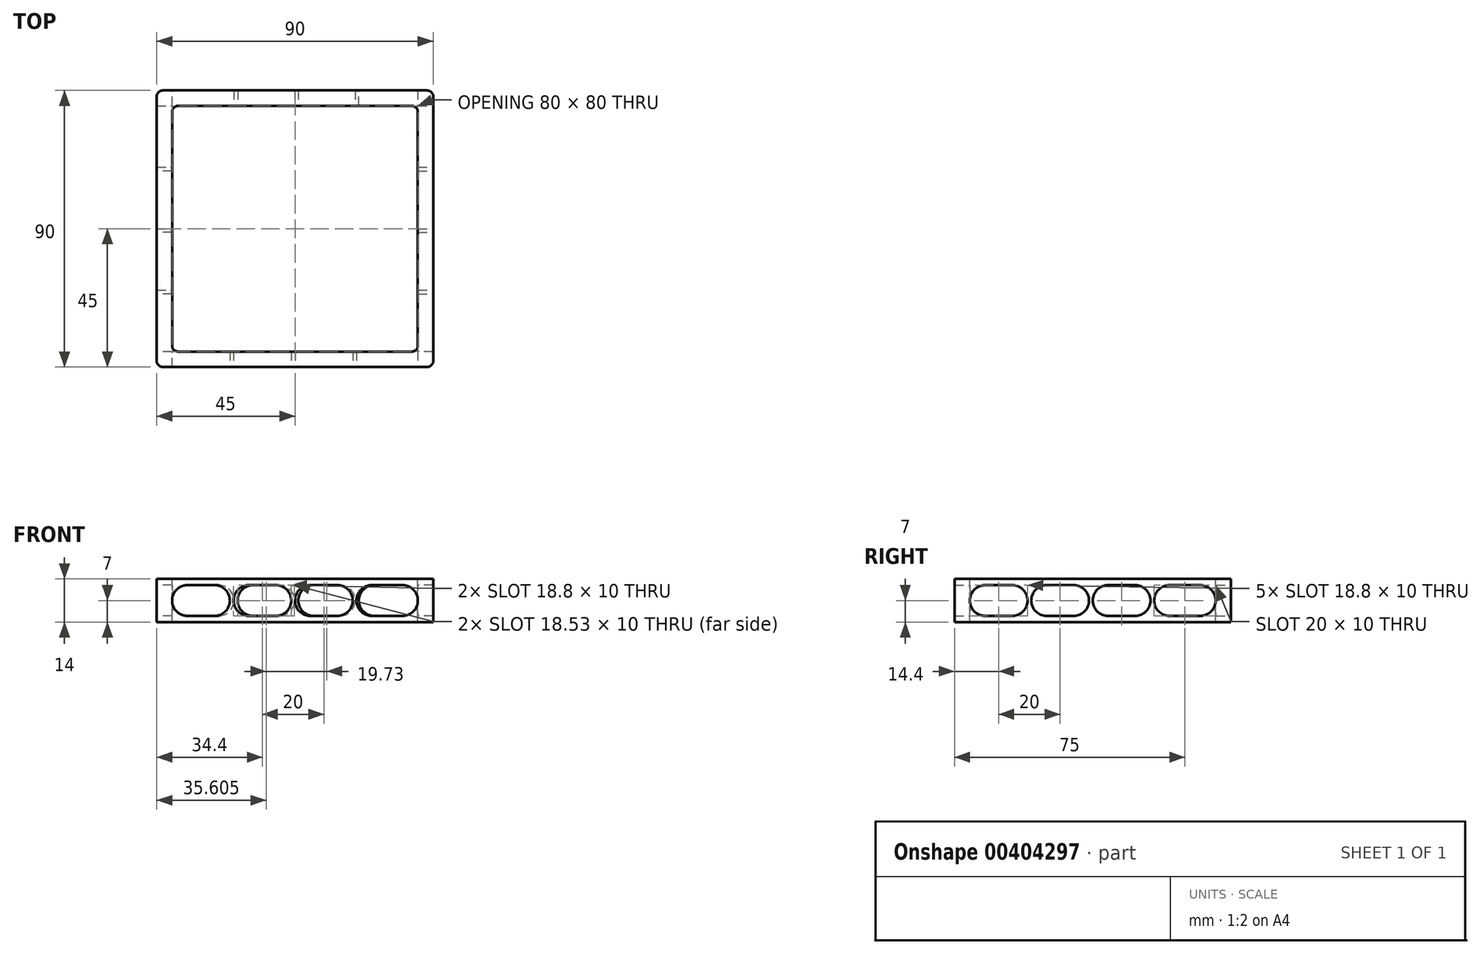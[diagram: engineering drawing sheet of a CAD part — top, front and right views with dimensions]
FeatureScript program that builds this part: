
annotation { "Feature Type Name" : "Feature", "Feature Type Description" : "" }
export const myFeature = defineFeature(function(context is Context, id is Id, definition is map)
    precondition{}
    {
        {
            var Q0;
            Q0=qCreatedBy(makeId("Front.planeOp"),FACE);
            var sketch = newSketch(context, id + "F0", { "sketchPlane" : qUnion([Q0])});
            skLineSegment(sketch, "E0.bottom", {"start": v(-45, 7) * mm, "end": v(45, 7) * mm});
            skLineSegment(sketch, "E0.top", {"start": v(-45, -7) * mm, "end": v(45, -7) * mm});
            skLineSegment(sketch, "E0.left", {"start": v(-45, 7) * mm, "end": v(-45, -7) * mm});
            skLineSegment(sketch, "E0.right", {"start": v(45, 7) * mm, "end": v(45, -7) * mm});
            skPoint(sketch, "E0.middle", {"position": v(0, 0) * mm});
            skSolve(sketch);
        }
        {
            var Q0;
            Q0=qSketchRegion(id+"F0",true);
            extrude(context, id + "F1", {"entities" : qUnion([Q0]), "endBound" : BoundingType.SYMMETRIC, "depth" : 90 * mm});
        }
        {
            var Q0;
            Q0=makeQuery(id+"F1.opExtrude","CAP_FACE",FACE,{"disambiguationData":[OSD([sQuery(id+"F0.wireOp",EDGE,"E0.bottom"),sQuery(id+"F0.wireOp",EDGE,"E0.top"),sQuery(id+"F0.wireOp",EDGE,"E0.left"),sQuery(id+"F0.wireOp",EDGE,"E0.right")])],"isStart":false});
            var sketch = newSketch(context, id + "F2", { "sketchPlane" : qUnion([Q0])});
            skLineSegment(sketch, "E1.bottom", {"start": v(-40, 5) * mm, "end": v(40, 5) * mm});
            skLineSegment(sketch, "E1.top", {"start": v(-40, -5) * mm, "end": v(40, -5) * mm});
            skLineSegment(sketch, "E1.left", {"start": v(-40, 5) * mm, "end": v(-40, -5) * mm});
            skLineSegment(sketch, "E1.right", {"start": v(40, 5) * mm, "end": v(40, -5) * mm});
            skPoint(sketch, "E1.middle", {"position": v(0, 0) * mm});
            skSolve(sketch);
        }
        {
            var Q0;
            Q0=qSketchRegion(id+"F2",true);
            extrude(context, id + "F3", {"entities" : qUnion([Q0]), "operationType" : NewBodyOperationType.REMOVE, "oppositeDirection" : true, "depth" : 90 * mm});
        }
        {
            var Q0;
            Q0=makeQuery(id+"F1.opExtrude","SWEPT_FACE",FACE,{"disambiguationData":[OSD([sQuery(id+"F0.wireOp",EDGE,"E0.right")])]});
            var sketch = newSketch(context, id + "F4", { "sketchPlane" : qUnion([Q0])});
            skLineSegment(sketch, "E2.bottom", {"start": v(-40, 5) * mm, "end": v(40, 5) * mm});
            skLineSegment(sketch, "E2.top", {"start": v(-40, -5) * mm, "end": v(40, -5) * mm});
            skLineSegment(sketch, "E2.left", {"start": v(-40, 5) * mm, "end": v(-40, -5) * mm});
            skLineSegment(sketch, "E2.right", {"start": v(40, 5) * mm, "end": v(40, -5) * mm});
            skPoint(sketch, "E2.middle", {"position": v(0, 0) * mm});
            skSolve(sketch);
        }
        {
            var Q0;
            Q0=qSketchRegion(id+"F4",true);
            extrude(context, id + "F5", {"entities" : qUnion([Q0]), "operationType" : NewBodyOperationType.REMOVE, "oppositeDirection" : true, "depth" : 90 * mm});
        }
        {
            var Q0;
            Q0=makeQuery(id+"F1.opExtrude","SWEPT_FACE",FACE,{"disambiguationData":[OSD([sQuery(id+"F0.wireOp",EDGE,"E0.bottom")])]});
            var sketch = newSketch(context, id + "F6", { "sketchPlane" : qUnion([Q0])});
            skLineSegment(sketch, "E3.bottom", {"start": v(-40, 40) * mm, "end": v(40, 40) * mm});
            skLineSegment(sketch, "E3.top", {"start": v(-40, -40) * mm, "end": v(40, -40) * mm});
            skLineSegment(sketch, "E3.left", {"start": v(-40, 40) * mm, "end": v(-40, -40) * mm});
            skLineSegment(sketch, "E3.right", {"start": v(40, 40) * mm, "end": v(40, -40) * mm});
            skSolve(sketch);
        }
        {
            var Q0;
            Q0=qSketchRegion(id+"F6",true);
            extrude(context, id + "F7", {"entities" : qUnion([Q0]), "operationType" : NewBodyOperationType.REMOVE, "oppositeDirection" : true, "depth" : 14 * mm});
        }
        {
            var Q0;
            {var subQ3=sQuery(id+"F6.wireOp",EDGE,"E3.bottom");var subQ4=sQuery(id+"F6.wireOp",EDGE,"E3.left");Q0=makeQuery(id+"F7.boolean.opBoolean","COPY",EDGE,{"disambiguationData":[TD([makeQuery(id+"F1.opExtrude","SWEPT_FACE",FACE,{"disambiguationData":[OSD([sQuery(id+"F0.wireOp",EDGE,"E0.bottom")])]})])],"derivedFrom":makeQuery(id+"F7.opExtrude","SWEPT_EDGE",EDGE,{"disambiguationData":[OSD([subQ3,subQ4])]})});}
            var Q1;
            {var subQ3=sQuery(id+"F6.wireOp",EDGE,"E3.bottom");var subQ4=sQuery(id+"F6.wireOp",EDGE,"E3.left");Q1=makeQuery(id+"F7.boolean.opBoolean","COPY",EDGE,{"disambiguationData":[TD([makeQuery(id+"F1.opExtrude","SWEPT_FACE",FACE,{"disambiguationData":[OSD([sQuery(id+"F0.wireOp",EDGE,"E0.top")])]})])],"derivedFrom":makeQuery(id+"F7.opExtrude","SWEPT_EDGE",EDGE,{"disambiguationData":[OSD([subQ3,subQ4])]})});}
            var Q2;
            {var subQ3=sQuery(id+"F6.wireOp",EDGE,"E3.top");var subQ4=sQuery(id+"F6.wireOp",EDGE,"E3.left");Q2=makeQuery(id+"F7.boolean.opBoolean","COPY",EDGE,{"disambiguationData":[TD([makeQuery(id+"F1.opExtrude","SWEPT_FACE",FACE,{"disambiguationData":[OSD([sQuery(id+"F0.wireOp",EDGE,"E0.top")])]})])],"derivedFrom":makeQuery(id+"F7.opExtrude","SWEPT_EDGE",EDGE,{"disambiguationData":[OSD([subQ3,subQ4])]})});}
            var Q3;
            {var subQ3=sQuery(id+"F6.wireOp",EDGE,"E3.top");var subQ4=sQuery(id+"F6.wireOp",EDGE,"E3.left");Q3=makeQuery(id+"F7.boolean.opBoolean","COPY",EDGE,{"disambiguationData":[TD([makeQuery(id+"F1.opExtrude","SWEPT_FACE",FACE,{"disambiguationData":[OSD([sQuery(id+"F0.wireOp",EDGE,"E0.bottom")])]})])],"derivedFrom":makeQuery(id+"F7.opExtrude","SWEPT_EDGE",EDGE,{"disambiguationData":[OSD([subQ3,subQ4])]})});}
            var Q4;
            {var subQ3=sQuery(id+"F6.wireOp",EDGE,"E3.right");var subQ4=sQuery(id+"F6.wireOp",EDGE,"E3.top");Q4=makeQuery(id+"F7.boolean.opBoolean","COPY",EDGE,{"disambiguationData":[TD([makeQuery(id+"F1.opExtrude","SWEPT_FACE",FACE,{"disambiguationData":[OSD([sQuery(id+"F0.wireOp",EDGE,"E0.bottom")])]})])],"derivedFrom":makeQuery(id+"F7.opExtrude","SWEPT_EDGE",EDGE,{"disambiguationData":[OSD([subQ4,subQ3])]})});}
            var Q5;
            {var subQ3=sQuery(id+"F6.wireOp",EDGE,"E3.top");var subQ4=sQuery(id+"F6.wireOp",EDGE,"E3.right");Q5=makeQuery(id+"F7.boolean.opBoolean","COPY",EDGE,{"disambiguationData":[TD([makeQuery(id+"F1.opExtrude","SWEPT_FACE",FACE,{"disambiguationData":[OSD([sQuery(id+"F0.wireOp",EDGE,"E0.top")])]})])],"derivedFrom":makeQuery(id+"F7.opExtrude","SWEPT_EDGE",EDGE,{"disambiguationData":[OSD([subQ3,subQ4])]})});}
            var Q6;
            {var subQ3=sQuery(id+"F6.wireOp",EDGE,"E3.right");var subQ4=sQuery(id+"F6.wireOp",EDGE,"E3.bottom");Q6=makeQuery(id+"F7.boolean.opBoolean","COPY",EDGE,{"disambiguationData":[TD([makeQuery(id+"F1.opExtrude","SWEPT_FACE",FACE,{"disambiguationData":[OSD([sQuery(id+"F0.wireOp",EDGE,"E0.bottom")])]})])],"derivedFrom":makeQuery(id+"F7.opExtrude","SWEPT_EDGE",EDGE,{"disambiguationData":[OSD([subQ4,subQ3])]})});}
            var Q7;
            {var subQ3=sQuery(id+"F6.wireOp",EDGE,"E3.bottom");var subQ4=sQuery(id+"F6.wireOp",EDGE,"E3.right");Q7=makeQuery(id+"F7.boolean.opBoolean","COPY",EDGE,{"disambiguationData":[TD([makeQuery(id+"F1.opExtrude","SWEPT_FACE",FACE,{"disambiguationData":[OSD([sQuery(id+"F0.wireOp",EDGE,"E0.top")])]})])],"derivedFrom":makeQuery(id+"F7.opExtrude","SWEPT_EDGE",EDGE,{"disambiguationData":[OSD([subQ3,subQ4])]})});}
            var Q8;
            Q8=makeQuery(id+"F1.opExtrude","CAP_EDGE",EDGE,{"disambiguationData":[OSD([sQuery(id+"F0.wireOp",EDGE,"E0.left")])],"isStart":false});
            var Q9;
            Q9=makeQuery(id+"F1.opExtrude","CAP_EDGE",EDGE,{"disambiguationData":[OSD([sQuery(id+"F0.wireOp",EDGE,"E0.right")])],"isStart":false});
            var Q10;
            Q10=makeQuery(id+"F1.opExtrude","CAP_EDGE",EDGE,{"disambiguationData":[OSD([sQuery(id+"F0.wireOp",EDGE,"E0.right")])],"isStart":true});
            var Q11;
            Q11=makeQuery(id+"F1.opExtrude","CAP_EDGE",EDGE,{"disambiguationData":[OSD([sQuery(id+"F0.wireOp",EDGE,"E0.left")])],"isStart":true});
            fillet(context, id + "F8", {"entities" : qUnion([Q0, Q1, Q2, Q3, Q4, Q5, Q6, Q7, Q8, Q9, Q10, Q11]), "radius" : 2 * mm, "allowEdgeOverflow" : false});
        }
        {
            var Q0;
            {var subQ0=sQuery(id+"F2.wireOp",EDGE,"E1.top");var subQ1=sQuery(id+"F2.wireOp",EDGE,"E1.right");Q0=makeQuery(id+"F5.boolean.opBoolean","SPLIT",EDGE,{"disambiguationData":[TD([makeQuery(id+"F5.opExtrude","SWEPT_FACE",FACE,{"disambiguationData":[OSD([sQuery(id+"F4.wireOp",EDGE,"E2.left")])]})])],"derivedFrom":makeQuery(id+"F3.boolean.opBoolean","COPY",EDGE,{"derivedFrom":makeQuery(id+"F3.opExtrude","SWEPT_EDGE",EDGE,{"disambiguationData":[OSD([subQ0,subQ1])]})})});}
            var Q1;
            {var subQ0=sQuery(id+"F2.wireOp",EDGE,"E1.bottom");var subQ1=sQuery(id+"F2.wireOp",EDGE,"E1.right");Q1=makeQuery(id+"F5.boolean.opBoolean","SPLIT",EDGE,{"disambiguationData":[TD([makeQuery(id+"F5.opExtrude","SWEPT_FACE",FACE,{"disambiguationData":[OSD([sQuery(id+"F4.wireOp",EDGE,"E2.left")])]})])],"derivedFrom":makeQuery(id+"F3.boolean.opBoolean","COPY",EDGE,{"derivedFrom":makeQuery(id+"F3.opExtrude","SWEPT_EDGE",EDGE,{"disambiguationData":[OSD([subQ0,subQ1])]})})});}
            var Q2;
            {var subQ0=sQuery(id+"F2.wireOp",EDGE,"E1.left");var subQ1=sQuery(id+"F2.wireOp",EDGE,"E1.top");Q2=makeQuery(id+"F5.boolean.opBoolean","SPLIT",EDGE,{"disambiguationData":[TD([makeQuery(id+"F5.opExtrude","SWEPT_FACE",FACE,{"disambiguationData":[OSD([sQuery(id+"F4.wireOp",EDGE,"E2.left")])]})])],"derivedFrom":makeQuery(id+"F3.boolean.opBoolean","COPY",EDGE,{"derivedFrom":makeQuery(id+"F3.opExtrude","SWEPT_EDGE",EDGE,{"disambiguationData":[OSD([subQ1,subQ0])]})})});}
            var Q3;
            {var subQ0=sQuery(id+"F2.wireOp",EDGE,"E1.left");var subQ1=sQuery(id+"F2.wireOp",EDGE,"E1.bottom");Q3=makeQuery(id+"F5.boolean.opBoolean","SPLIT",EDGE,{"disambiguationData":[TD([makeQuery(id+"F5.opExtrude","SWEPT_FACE",FACE,{"disambiguationData":[OSD([sQuery(id+"F4.wireOp",EDGE,"E2.left")])]})])],"derivedFrom":makeQuery(id+"F3.boolean.opBoolean","COPY",EDGE,{"derivedFrom":makeQuery(id+"F3.opExtrude","SWEPT_EDGE",EDGE,{"disambiguationData":[OSD([subQ1,subQ0])]})})});}
            var Q4;
            {var subQ0=sQuery(id+"F4.wireOp",EDGE,"E2.top");var subQ1=sQuery(id+"F4.wireOp",EDGE,"E2.left");Q4=makeQuery(id+"F5.boolean.opBoolean","COPY",EDGE,{"disambiguationData":[TD([makeQuery(id+"F1.opExtrude","SWEPT_FACE",FACE,{"disambiguationData":[OSD([sQuery(id+"F0.wireOp",EDGE,"E0.right")])]})])],"derivedFrom":makeQuery(id+"F5.opExtrude","SWEPT_EDGE",EDGE,{"disambiguationData":[OSD([subQ0,subQ1])]})});}
            var Q5;
            {var subQ0=sQuery(id+"F4.wireOp",EDGE,"E2.bottom");var subQ1=sQuery(id+"F4.wireOp",EDGE,"E2.left");Q5=makeQuery(id+"F5.boolean.opBoolean","COPY",EDGE,{"disambiguationData":[TD([makeQuery(id+"F1.opExtrude","SWEPT_FACE",FACE,{"disambiguationData":[OSD([sQuery(id+"F0.wireOp",EDGE,"E0.right")])]})])],"derivedFrom":makeQuery(id+"F5.opExtrude","SWEPT_EDGE",EDGE,{"disambiguationData":[OSD([subQ0,subQ1])]})});}
            var Q6;
            {var subQ0=sQuery(id+"F4.wireOp",EDGE,"E2.top");var subQ1=sQuery(id+"F4.wireOp",EDGE,"E2.right");Q6=makeQuery(id+"F5.boolean.opBoolean","COPY",EDGE,{"disambiguationData":[TD([makeQuery(id+"F1.opExtrude","SWEPT_FACE",FACE,{"disambiguationData":[OSD([sQuery(id+"F0.wireOp",EDGE,"E0.right")])]})])],"derivedFrom":makeQuery(id+"F5.opExtrude","SWEPT_EDGE",EDGE,{"disambiguationData":[OSD([subQ0,subQ1])]})});}
            var Q7;
            {var subQ0=sQuery(id+"F4.wireOp",EDGE,"E2.bottom");var subQ1=sQuery(id+"F4.wireOp",EDGE,"E2.right");Q7=makeQuery(id+"F5.boolean.opBoolean","COPY",EDGE,{"disambiguationData":[TD([makeQuery(id+"F1.opExtrude","SWEPT_FACE",FACE,{"disambiguationData":[OSD([sQuery(id+"F0.wireOp",EDGE,"E0.right")])]})])],"derivedFrom":makeQuery(id+"F5.opExtrude","SWEPT_EDGE",EDGE,{"disambiguationData":[OSD([subQ0,subQ1])]})});}
            var Q8;
            {var subQ0=sQuery(id+"F2.wireOp",EDGE,"E1.right");var subQ1=sQuery(id+"F2.wireOp",EDGE,"E1.top");Q8=makeQuery(id+"F5.boolean.opBoolean","SPLIT",EDGE,{"disambiguationData":[TD([makeQuery(id+"F5.opExtrude","SWEPT_FACE",FACE,{"disambiguationData":[OSD([sQuery(id+"F4.wireOp",EDGE,"E2.right")])]})])],"derivedFrom":makeQuery(id+"F3.boolean.opBoolean","COPY",EDGE,{"derivedFrom":makeQuery(id+"F3.opExtrude","SWEPT_EDGE",EDGE,{"disambiguationData":[OSD([subQ1,subQ0])]})})});}
            var Q9;
            {var subQ0=sQuery(id+"F2.wireOp",EDGE,"E1.right");var subQ1=sQuery(id+"F2.wireOp",EDGE,"E1.bottom");Q9=makeQuery(id+"F5.boolean.opBoolean","SPLIT",EDGE,{"disambiguationData":[TD([makeQuery(id+"F5.opExtrude","SWEPT_FACE",FACE,{"disambiguationData":[OSD([sQuery(id+"F4.wireOp",EDGE,"E2.right")])]})])],"derivedFrom":makeQuery(id+"F3.boolean.opBoolean","COPY",EDGE,{"derivedFrom":makeQuery(id+"F3.opExtrude","SWEPT_EDGE",EDGE,{"disambiguationData":[OSD([subQ1,subQ0])]})})});}
            var Q10;
            {var subQ0=sQuery(id+"F2.wireOp",EDGE,"E1.top");var subQ1=sQuery(id+"F2.wireOp",EDGE,"E1.left");Q10=makeQuery(id+"F5.boolean.opBoolean","SPLIT",EDGE,{"disambiguationData":[TD([makeQuery(id+"F5.opExtrude","SWEPT_FACE",FACE,{"disambiguationData":[OSD([sQuery(id+"F4.wireOp",EDGE,"E2.right")])]})])],"derivedFrom":makeQuery(id+"F3.boolean.opBoolean","COPY",EDGE,{"derivedFrom":makeQuery(id+"F3.opExtrude","SWEPT_EDGE",EDGE,{"disambiguationData":[OSD([subQ0,subQ1])]})})});}
            var Q11;
            {var subQ0=sQuery(id+"F4.wireOp",EDGE,"E2.top");var subQ1=sQuery(id+"F4.wireOp",EDGE,"E2.right");Q11=makeQuery(id+"F5.boolean.opBoolean","COPY",EDGE,{"disambiguationData":[TD([makeQuery(id+"F1.opExtrude","SWEPT_FACE",FACE,{"disambiguationData":[OSD([sQuery(id+"F0.wireOp",EDGE,"E0.left")])]})])],"derivedFrom":makeQuery(id+"F5.opExtrude","SWEPT_EDGE",EDGE,{"disambiguationData":[OSD([subQ0,subQ1])]})});}
            var Q12;
            {var subQ0=sQuery(id+"F4.wireOp",EDGE,"E2.top");var subQ1=sQuery(id+"F4.wireOp",EDGE,"E2.left");Q12=makeQuery(id+"F5.boolean.opBoolean","COPY",EDGE,{"disambiguationData":[TD([makeQuery(id+"F1.opExtrude","SWEPT_FACE",FACE,{"disambiguationData":[OSD([sQuery(id+"F0.wireOp",EDGE,"E0.left")])]})])],"derivedFrom":makeQuery(id+"F5.opExtrude","SWEPT_EDGE",EDGE,{"disambiguationData":[OSD([subQ0,subQ1])]})});}
            var Q13;
            {var subQ0=sQuery(id+"F4.wireOp",EDGE,"E2.bottom");var subQ1=sQuery(id+"F4.wireOp",EDGE,"E2.left");Q13=makeQuery(id+"F5.boolean.opBoolean","COPY",EDGE,{"disambiguationData":[TD([makeQuery(id+"F1.opExtrude","SWEPT_FACE",FACE,{"disambiguationData":[OSD([sQuery(id+"F0.wireOp",EDGE,"E0.left")])]})])],"derivedFrom":makeQuery(id+"F5.opExtrude","SWEPT_EDGE",EDGE,{"disambiguationData":[OSD([subQ0,subQ1])]})});}
            var Q14;
            {var subQ0=sQuery(id+"F2.wireOp",EDGE,"E1.bottom");var subQ1=sQuery(id+"F2.wireOp",EDGE,"E1.left");Q14=makeQuery(id+"F5.boolean.opBoolean","SPLIT",EDGE,{"disambiguationData":[TD([makeQuery(id+"F5.opExtrude","SWEPT_FACE",FACE,{"disambiguationData":[OSD([sQuery(id+"F4.wireOp",EDGE,"E2.right")])]})])],"derivedFrom":makeQuery(id+"F3.boolean.opBoolean","COPY",EDGE,{"derivedFrom":makeQuery(id+"F3.opExtrude","SWEPT_EDGE",EDGE,{"disambiguationData":[OSD([subQ0,subQ1])]})})});}
            var Q15;
            {var subQ0=sQuery(id+"F4.wireOp",EDGE,"E2.bottom");var subQ1=sQuery(id+"F4.wireOp",EDGE,"E2.right");Q15=makeQuery(id+"F5.boolean.opBoolean","COPY",EDGE,{"disambiguationData":[TD([makeQuery(id+"F1.opExtrude","SWEPT_FACE",FACE,{"disambiguationData":[OSD([sQuery(id+"F0.wireOp",EDGE,"E0.left")])]})])],"derivedFrom":makeQuery(id+"F5.opExtrude","SWEPT_EDGE",EDGE,{"disambiguationData":[OSD([subQ0,subQ1])]})});}
            fillet(context, id + "F9", {"entities" : qUnion([Q0, Q1, Q2, Q3, Q4, Q5, Q6, Q7, Q8, Q9, Q10, Q11, Q12, Q13, Q14, Q15]), "radius" : 5 * mm, "tangentPropagation" : true, "allowEdgeOverflow" : false});
        }
        {
            var Q0;
            Q0=makeQuery(id+"F1.opExtrude","SWEPT_FACE",FACE,{"disambiguationData":[OSD([sQuery(id+"F0.wireOp",EDGE,"E0.bottom")])]});
            var sketch = newSketch(context, id + "F10", { "sketchPlane" : qUnion([Q0])});
            skLineSegment(sketch, "E4.bottom", {"start": v(18.8, -40) * mm, "end": v(20, -40) * mm});
            skLineSegment(sketch, "E4.top", {"start": v(18.8, -45) * mm, "end": v(20, -45) * mm});
            skLineSegment(sketch, "E4.left", {"start": v(18.8, -40) * mm, "end": v(18.8, -45) * mm});
            skLineSegment(sketch, "E4.right", {"start": v(20, -40) * mm, "end": v(20, -45) * mm});
            skLineSegment(sketch, "E5.1.0.0", {"start": v(-1.2, -40) * mm, "end": v(-1.2, -45) * mm});
            skLineSegment(sketch, "E5.1.0.1", {"start": v(0, -40) * mm, "end": v(0, -45) * mm});
            skLineSegment(sketch, "E5.1.0.2", {"start": v(-1.2, -45) * mm, "end": v(0, -45) * mm});
            skLineSegment(sketch, "E5.1.0.3", {"start": v(-1.2, -40) * mm, "end": v(0, -40) * mm});
            skLineSegment(sketch, "E5.2.0.0", {"start": v(-21.2, -40) * mm, "end": v(-21.2, -45) * mm});
            skLineSegment(sketch, "E5.2.0.1", {"start": v(-20, -40) * mm, "end": v(-20, -45) * mm});
            skLineSegment(sketch, "E5.2.0.2", {"start": v(-21.2, -45) * mm, "end": v(-20, -45) * mm});
            skLineSegment(sketch, "E5.2.0.3", {"start": v(-21.2, -40) * mm, "end": v(-20, -40) * mm});
            skLineSegment(sketch, "E5.direction1", {"start": v(18.8, -45) * mm, "end": v(-1.2, -45) * mm, "construction": true});
            skLineSegment(sketch, "E6.0.1.0", {"start": v(19.6, 40) * mm, "end": v(-0.13, 40) * mm, "construction": true});
            skLineSegment(sketch, "E6.0.1.1", {"start": v(19.6, 40) * mm, "end": v(20.8, 40) * mm});
            skLineSegment(sketch, "E6.0.1.2", {"start": v(19.6, 45) * mm, "end": v(19.6, 40) * mm});
            skLineSegment(sketch, "E6.0.1.3", {"start": v(20.8, 45) * mm, "end": v(20.8, 40) * mm});
            skLineSegment(sketch, "E6.0.1.4", {"start": v(-29.6, 40) * mm, "end": v(-29.2, 40) * mm});
            skLineSegment(sketch, "E6.0.1.5", {"start": v(-29.6, 45) * mm, "end": v(-29.2, 45) * mm});
            skLineSegment(sketch, "E6.0.1.6", {"start": v(19.6, 45) * mm, "end": v(20.8, 45) * mm});
            skLineSegment(sketch, "E6.0.1.7", {"start": v(1.07, 45) * mm, "end": v(1.07, 40) * mm});
            skLineSegment(sketch, "E6.0.1.8", {"start": v(-0.13, 45) * mm, "end": v(1.07, 45) * mm});
            skLineSegment(sketch, "E6.0.1.9", {"start": v(-18.66, 45) * mm, "end": v(-18.66, 40) * mm});
            skLineSegment(sketch, "E6.0.1.10", {"start": v(-19.86, 40) * mm, "end": v(-18.66, 40) * mm});
            skLineSegment(sketch, "E6.0.1.11", {"start": v(-19.86, 45) * mm, "end": v(-18.66, 45) * mm});
            skLineSegment(sketch, "E6.0.1.14", {"start": v(-0.13, 45) * mm, "end": v(-0.13, 40) * mm});
            skLineSegment(sketch, "E6.0.1.15", {"start": v(-0.13, 40) * mm, "end": v(1.07, 40) * mm});
            skLineSegment(sketch, "E6.0.1.16", {"start": v(-19.86, 45) * mm, "end": v(-19.86, 40) * mm});
            skLineSegment(sketch, "E6.direction1", {"start": v(-29.6, -45) * mm, "end": v(-5, -45) * mm, "construction": true});
            skLineSegment(sketch, "E7.bottom", {"start": v(40, 18.8) * mm, "end": v(45, 18.8) * mm});
            skLineSegment(sketch, "E7.top", {"start": v(40, 20) * mm, "end": v(45, 20) * mm});
            skLineSegment(sketch, "E7.left", {"start": v(40, 18.8) * mm, "end": v(40, 20) * mm});
            skLineSegment(sketch, "E7.right", {"start": v(45, 18.8) * mm, "end": v(45, 20) * mm});
            skLineSegment(sketch, "E8.0.1.0", {"start": v(40, 0) * mm, "end": v(45, 0) * mm});
            skLineSegment(sketch, "E8.0.1.1", {"start": v(40, -1.2) * mm, "end": v(45, -1.2) * mm});
            skLineSegment(sketch, "E8.0.1.2", {"start": v(45, -1.2) * mm, "end": v(45, 0) * mm});
            skLineSegment(sketch, "E8.0.1.3", {"start": v(40, -1.2) * mm, "end": v(40, 0) * mm});
            skLineSegment(sketch, "E8.0.2.0", {"start": v(40, -20) * mm, "end": v(45, -20) * mm});
            skLineSegment(sketch, "E8.0.2.1", {"start": v(40, -21.2) * mm, "end": v(45, -21.2) * mm});
            skLineSegment(sketch, "E8.0.2.2", {"start": v(45, -21.2) * mm, "end": v(45, -20) * mm});
            skLineSegment(sketch, "E8.0.2.3", {"start": v(40, -21.2) * mm, "end": v(40, -20) * mm});
            skLineSegment(sketch, "E8.1.0.0", {"start": v(-45, 20) * mm, "end": v(-40, 20) * mm});
            skLineSegment(sketch, "E8.1.0.1", {"start": v(-45, 18.8) * mm, "end": v(-40, 18.8) * mm});
            skLineSegment(sketch, "E8.1.0.2", {"start": v(-40, 18.8) * mm, "end": v(-40, 20) * mm});
            skLineSegment(sketch, "E8.1.0.3", {"start": v(-45, 18.8) * mm, "end": v(-45, 20) * mm});
            skLineSegment(sketch, "E8.1.1.0", {"start": v(-45, 0) * mm, "end": v(-40, 0) * mm});
            skLineSegment(sketch, "E8.1.1.1", {"start": v(-45, -1.2) * mm, "end": v(-40, -1.2) * mm});
            skLineSegment(sketch, "E8.1.1.2", {"start": v(-40, -1.2) * mm, "end": v(-40, 0) * mm});
            skLineSegment(sketch, "E8.1.1.3", {"start": v(-45, -1.2) * mm, "end": v(-45, 0) * mm});
            skLineSegment(sketch, "E8.1.2.0", {"start": v(-45, -20) * mm, "end": v(-40, -20) * mm});
            skLineSegment(sketch, "E8.1.2.1", {"start": v(-45, -21.2) * mm, "end": v(-40, -21.2) * mm});
            skLineSegment(sketch, "E8.1.2.2", {"start": v(-40, -21.2) * mm, "end": v(-40, -20) * mm});
            skLineSegment(sketch, "E8.1.2.3", {"start": v(-45, -21.2) * mm, "end": v(-45, -20) * mm});
            skLineSegment(sketch, "E8.direction1", {"start": v(40, 18.8) * mm, "end": v(-45, 18.8) * mm, "construction": true});
            skLineSegment(sketch, "E8.direction2", {"start": v(40, 18.8) * mm, "end": v(40, -1.2) * mm, "construction": true});
            skSolve(sketch);
        }
        {
            var Q0;
            Q0=qSketchRegion(id+"F10",true);
            extrude(context, id + "F11", {"entities" : qUnion([Q0]), "operationType" : NewBodyOperationType.ADD, "oppositeDirection" : true, "depth" : 14 * mm});
        }
        {
            var Q0;
            {var subQ1=makeQuery(id+"F5.opExtrude","SWEPT_FACE",FACE,{"disambiguationData":[OSD([sQuery(id+"F4.wireOp",EDGE,"E2.top")])]});var subQ2=makeQuery(id+"F3.boolean.opBoolean","COPY",FACE,{"derivedFrom":makeQuery(id+"F3.opExtrude","SWEPT_FACE",FACE,{"disambiguationData":[OSD([sQuery(id+"F2.wireOp",EDGE,"E1.top")])]})});var subQ3=sQuery(id+"F0.wireOp",EDGE,"E0.left");var subQ4=makeQuery(id+"F1.opExtrude","SWEPT_FACE",FACE,{"disambiguationData":[OSD([subQ3])]});var subQ14=makeQuery(id+"F5.boolean.opBoolean","MERGE",FACE,{"derivedFrom":[subQ2,subQ1]});var subQ16=sQuery(id+"F0.wireOp",EDGE,"E0.right");var subQ17=makeQuery(id+"F1.opExtrude","SWEPT_FACE",FACE,{"disambiguationData":[OSD([subQ16])]});var subQ21=sQuery(id+"F0.wireOp",EDGE,"E0.top");var subQ22=sQuery(id+"F0.wireOp",EDGE,"E0.bottom");Q0=makeQuery(id+"F11.boolean.opBoolean","INTERSECT",EDGE,{"derivedFrom":[makeQuery(id+"F9.opFillet","SPLIT",FACE,{"disambiguationData":[OD(0.0)],"derivedFrom":makeQuery(id+"F8.opFillet","MERGE",FACE,{"derivedFrom":[makeQuery(id+"F7.boolean.opBoolean","SPLIT",FACE,{"disambiguationData":[TD([makeQuery(id+"F1.opExtrude","CAP_FACE",FACE,{"disambiguationData":[OSD([subQ22,subQ21,subQ3,subQ16])],"isStart":false})])],"derivedFrom":subQ14}),makeQuery(id+"F7.boolean.opBoolean","SPLIT",FACE,{"disambiguationData":[TD([makeQuery(id+"F1.opExtrude","CAP_FACE",FACE,{"disambiguationData":[OSD([subQ22,subQ21,subQ3,subQ16])],"isStart":true})])],"derivedFrom":subQ14}),makeQuery(id+"F7.boolean.opBoolean","SPLIT",FACE,{"disambiguationData":[TD([subQ17])],"derivedFrom":subQ14}),makeQuery(id+"F7.boolean.opBoolean","SPLIT",FACE,{"disambiguationData":[TD([subQ4])],"derivedFrom":subQ14})]})}),makeQuery(id+"F11.opExtrude","SWEPT_FACE",FACE,{"disambiguationData":[OSD([sQuery(id+"F10.wireOp",EDGE,"E4.right")])]})]});}
            var Q1;
            {var subQ1=makeQuery(id+"F5.opExtrude","SWEPT_FACE",FACE,{"disambiguationData":[OSD([sQuery(id+"F4.wireOp",EDGE,"E2.top")])]});var subQ2=makeQuery(id+"F3.boolean.opBoolean","COPY",FACE,{"derivedFrom":makeQuery(id+"F3.opExtrude","SWEPT_FACE",FACE,{"disambiguationData":[OSD([sQuery(id+"F2.wireOp",EDGE,"E1.top")])]})});var subQ3=sQuery(id+"F0.wireOp",EDGE,"E0.left");var subQ4=makeQuery(id+"F1.opExtrude","SWEPT_FACE",FACE,{"disambiguationData":[OSD([subQ3])]});var subQ14=makeQuery(id+"F5.boolean.opBoolean","MERGE",FACE,{"derivedFrom":[subQ2,subQ1]});var subQ16=sQuery(id+"F0.wireOp",EDGE,"E0.right");var subQ17=makeQuery(id+"F1.opExtrude","SWEPT_FACE",FACE,{"disambiguationData":[OSD([subQ16])]});var subQ21=sQuery(id+"F0.wireOp",EDGE,"E0.top");var subQ22=sQuery(id+"F0.wireOp",EDGE,"E0.bottom");Q1=makeQuery(id+"F11.boolean.opBoolean","INTERSECT",EDGE,{"derivedFrom":[makeQuery(id+"F9.opFillet","SPLIT",FACE,{"disambiguationData":[OD(0.0)],"derivedFrom":makeQuery(id+"F8.opFillet","MERGE",FACE,{"derivedFrom":[makeQuery(id+"F7.boolean.opBoolean","SPLIT",FACE,{"disambiguationData":[TD([makeQuery(id+"F1.opExtrude","CAP_FACE",FACE,{"disambiguationData":[OSD([subQ22,subQ21,subQ3,subQ16])],"isStart":false})])],"derivedFrom":subQ14}),makeQuery(id+"F7.boolean.opBoolean","SPLIT",FACE,{"disambiguationData":[TD([makeQuery(id+"F1.opExtrude","CAP_FACE",FACE,{"disambiguationData":[OSD([subQ22,subQ21,subQ3,subQ16])],"isStart":true})])],"derivedFrom":subQ14}),makeQuery(id+"F7.boolean.opBoolean","SPLIT",FACE,{"disambiguationData":[TD([subQ17])],"derivedFrom":subQ14}),makeQuery(id+"F7.boolean.opBoolean","SPLIT",FACE,{"disambiguationData":[TD([subQ4])],"derivedFrom":subQ14})]})}),makeQuery(id+"F11.opExtrude","SWEPT_FACE",FACE,{"disambiguationData":[OSD([sQuery(id+"F10.wireOp",EDGE,"E5.1.0.1")])]})]});}
            var Q2;
            {var subQ1=makeQuery(id+"F5.opExtrude","SWEPT_FACE",FACE,{"disambiguationData":[OSD([sQuery(id+"F4.wireOp",EDGE,"E2.top")])]});var subQ2=makeQuery(id+"F3.boolean.opBoolean","COPY",FACE,{"derivedFrom":makeQuery(id+"F3.opExtrude","SWEPT_FACE",FACE,{"disambiguationData":[OSD([sQuery(id+"F2.wireOp",EDGE,"E1.top")])]})});var subQ3=sQuery(id+"F0.wireOp",EDGE,"E0.left");var subQ4=makeQuery(id+"F1.opExtrude","SWEPT_FACE",FACE,{"disambiguationData":[OSD([subQ3])]});var subQ14=makeQuery(id+"F5.boolean.opBoolean","MERGE",FACE,{"derivedFrom":[subQ2,subQ1]});var subQ16=sQuery(id+"F0.wireOp",EDGE,"E0.right");var subQ17=makeQuery(id+"F1.opExtrude","SWEPT_FACE",FACE,{"disambiguationData":[OSD([subQ16])]});var subQ21=sQuery(id+"F0.wireOp",EDGE,"E0.top");var subQ22=sQuery(id+"F0.wireOp",EDGE,"E0.bottom");Q2=makeQuery(id+"F11.boolean.opBoolean","INTERSECT",EDGE,{"derivedFrom":[makeQuery(id+"F9.opFillet","SPLIT",FACE,{"disambiguationData":[OD(0.0)],"derivedFrom":makeQuery(id+"F8.opFillet","MERGE",FACE,{"derivedFrom":[makeQuery(id+"F7.boolean.opBoolean","SPLIT",FACE,{"disambiguationData":[TD([makeQuery(id+"F1.opExtrude","CAP_FACE",FACE,{"disambiguationData":[OSD([subQ22,subQ21,subQ3,subQ16])],"isStart":false})])],"derivedFrom":subQ14}),makeQuery(id+"F7.boolean.opBoolean","SPLIT",FACE,{"disambiguationData":[TD([makeQuery(id+"F1.opExtrude","CAP_FACE",FACE,{"disambiguationData":[OSD([subQ22,subQ21,subQ3,subQ16])],"isStart":true})])],"derivedFrom":subQ14}),makeQuery(id+"F7.boolean.opBoolean","SPLIT",FACE,{"disambiguationData":[TD([subQ17])],"derivedFrom":subQ14}),makeQuery(id+"F7.boolean.opBoolean","SPLIT",FACE,{"disambiguationData":[TD([subQ4])],"derivedFrom":subQ14})]})}),makeQuery(id+"F11.opExtrude","SWEPT_FACE",FACE,{"disambiguationData":[OSD([sQuery(id+"F10.wireOp",EDGE,"E5.2.0.1")])]})]});}
            var Q3;
            {var subQ1=makeQuery(id+"F5.opExtrude","SWEPT_FACE",FACE,{"disambiguationData":[OSD([sQuery(id+"F4.wireOp",EDGE,"E2.top")])]});var subQ2=makeQuery(id+"F3.boolean.opBoolean","COPY",FACE,{"derivedFrom":makeQuery(id+"F3.opExtrude","SWEPT_FACE",FACE,{"disambiguationData":[OSD([sQuery(id+"F2.wireOp",EDGE,"E1.top")])]})});var subQ3=sQuery(id+"F0.wireOp",EDGE,"E0.left");var subQ4=makeQuery(id+"F1.opExtrude","SWEPT_FACE",FACE,{"disambiguationData":[OSD([subQ3])]});var subQ14=makeQuery(id+"F5.boolean.opBoolean","MERGE",FACE,{"derivedFrom":[subQ2,subQ1]});var subQ16=sQuery(id+"F0.wireOp",EDGE,"E0.right");var subQ17=makeQuery(id+"F1.opExtrude","SWEPT_FACE",FACE,{"disambiguationData":[OSD([subQ16])]});var subQ21=sQuery(id+"F0.wireOp",EDGE,"E0.top");var subQ22=sQuery(id+"F0.wireOp",EDGE,"E0.bottom");Q3=makeQuery(id+"F11.boolean.opBoolean","INTERSECT",EDGE,{"derivedFrom":[makeQuery(id+"F9.opFillet","SPLIT",FACE,{"disambiguationData":[OD(1.0)],"derivedFrom":makeQuery(id+"F8.opFillet","MERGE",FACE,{"derivedFrom":[makeQuery(id+"F7.boolean.opBoolean","SPLIT",FACE,{"disambiguationData":[TD([makeQuery(id+"F1.opExtrude","CAP_FACE",FACE,{"disambiguationData":[OSD([subQ22,subQ21,subQ3,subQ16])],"isStart":false})])],"derivedFrom":subQ14}),makeQuery(id+"F7.boolean.opBoolean","SPLIT",FACE,{"disambiguationData":[TD([makeQuery(id+"F1.opExtrude","CAP_FACE",FACE,{"disambiguationData":[OSD([subQ22,subQ21,subQ3,subQ16])],"isStart":true})])],"derivedFrom":subQ14}),makeQuery(id+"F7.boolean.opBoolean","SPLIT",FACE,{"disambiguationData":[TD([subQ17])],"derivedFrom":subQ14}),makeQuery(id+"F7.boolean.opBoolean","SPLIT",FACE,{"disambiguationData":[TD([subQ4])],"derivedFrom":subQ14})]})}),makeQuery(id+"F11.opExtrude","SWEPT_FACE",FACE,{"disambiguationData":[OSD([sQuery(id+"F10.wireOp",EDGE,"E6.0.1.9")])]})]});}
            var Q4;
            {var subQ1=makeQuery(id+"F5.opExtrude","SWEPT_FACE",FACE,{"disambiguationData":[OSD([sQuery(id+"F4.wireOp",EDGE,"E2.top")])]});var subQ2=makeQuery(id+"F3.boolean.opBoolean","COPY",FACE,{"derivedFrom":makeQuery(id+"F3.opExtrude","SWEPT_FACE",FACE,{"disambiguationData":[OSD([sQuery(id+"F2.wireOp",EDGE,"E1.top")])]})});var subQ3=sQuery(id+"F0.wireOp",EDGE,"E0.left");var subQ4=makeQuery(id+"F1.opExtrude","SWEPT_FACE",FACE,{"disambiguationData":[OSD([subQ3])]});var subQ14=makeQuery(id+"F5.boolean.opBoolean","MERGE",FACE,{"derivedFrom":[subQ2,subQ1]});var subQ16=sQuery(id+"F0.wireOp",EDGE,"E0.right");var subQ17=makeQuery(id+"F1.opExtrude","SWEPT_FACE",FACE,{"disambiguationData":[OSD([subQ16])]});var subQ21=sQuery(id+"F0.wireOp",EDGE,"E0.top");var subQ22=sQuery(id+"F0.wireOp",EDGE,"E0.bottom");Q4=makeQuery(id+"F11.boolean.opBoolean","INTERSECT",EDGE,{"derivedFrom":[makeQuery(id+"F9.opFillet","SPLIT",FACE,{"disambiguationData":[OD(1.0)],"derivedFrom":makeQuery(id+"F8.opFillet","MERGE",FACE,{"derivedFrom":[makeQuery(id+"F7.boolean.opBoolean","SPLIT",FACE,{"disambiguationData":[TD([makeQuery(id+"F1.opExtrude","CAP_FACE",FACE,{"disambiguationData":[OSD([subQ22,subQ21,subQ3,subQ16])],"isStart":false})])],"derivedFrom":subQ14}),makeQuery(id+"F7.boolean.opBoolean","SPLIT",FACE,{"disambiguationData":[TD([makeQuery(id+"F1.opExtrude","CAP_FACE",FACE,{"disambiguationData":[OSD([subQ22,subQ21,subQ3,subQ16])],"isStart":true})])],"derivedFrom":subQ14}),makeQuery(id+"F7.boolean.opBoolean","SPLIT",FACE,{"disambiguationData":[TD([subQ17])],"derivedFrom":subQ14}),makeQuery(id+"F7.boolean.opBoolean","SPLIT",FACE,{"disambiguationData":[TD([subQ4])],"derivedFrom":subQ14})]})}),makeQuery(id+"F11.opExtrude","SWEPT_FACE",FACE,{"disambiguationData":[OSD([sQuery(id+"F10.wireOp",EDGE,"E6.0.1.7")])]})]});}
            var Q5;
            {var subQ0=makeQuery(id+"F5.opExtrude","SWEPT_FACE",FACE,{"disambiguationData":[OSD([sQuery(id+"F4.wireOp",EDGE,"E2.bottom")])]});var subQ2=makeQuery(id+"F3.boolean.opBoolean","COPY",FACE,{"derivedFrom":makeQuery(id+"F3.opExtrude","SWEPT_FACE",FACE,{"disambiguationData":[OSD([sQuery(id+"F2.wireOp",EDGE,"E1.bottom")])]})});var subQ3=sQuery(id+"F0.wireOp",EDGE,"E0.left");var subQ4=makeQuery(id+"F1.opExtrude","SWEPT_FACE",FACE,{"disambiguationData":[OSD([subQ3])]});var subQ14=makeQuery(id+"F5.boolean.opBoolean","MERGE",FACE,{"derivedFrom":[subQ2,subQ0]});var subQ16=sQuery(id+"F0.wireOp",EDGE,"E0.right");var subQ17=makeQuery(id+"F1.opExtrude","SWEPT_FACE",FACE,{"disambiguationData":[OSD([subQ16])]});var subQ21=sQuery(id+"F0.wireOp",EDGE,"E0.top");var subQ22=sQuery(id+"F0.wireOp",EDGE,"E0.bottom");Q5=makeQuery(id+"F11.boolean.opBoolean","INTERSECT",EDGE,{"derivedFrom":[makeQuery(id+"F9.opFillet","SPLIT",FACE,{"disambiguationData":[OD(0.0)],"derivedFrom":makeQuery(id+"F8.opFillet","MERGE",FACE,{"derivedFrom":[makeQuery(id+"F7.boolean.opBoolean","SPLIT",FACE,{"disambiguationData":[TD([makeQuery(id+"F1.opExtrude","CAP_FACE",FACE,{"disambiguationData":[OSD([subQ22,subQ21,subQ3,subQ16])],"isStart":false})])],"derivedFrom":subQ14}),makeQuery(id+"F7.boolean.opBoolean","SPLIT",FACE,{"disambiguationData":[TD([makeQuery(id+"F1.opExtrude","CAP_FACE",FACE,{"disambiguationData":[OSD([subQ22,subQ21,subQ3,subQ16])],"isStart":true})])],"derivedFrom":subQ14}),makeQuery(id+"F7.boolean.opBoolean","SPLIT",FACE,{"disambiguationData":[TD([subQ17])],"derivedFrom":subQ14}),makeQuery(id+"F7.boolean.opBoolean","SPLIT",FACE,{"disambiguationData":[TD([subQ4])],"derivedFrom":subQ14})]})}),makeQuery(id+"F11.opExtrude","SWEPT_FACE",FACE,{"disambiguationData":[OSD([sQuery(id+"F10.wireOp",EDGE,"E4.right")])]})]});}
            var Q6;
            {var subQ0=makeQuery(id+"F5.opExtrude","SWEPT_FACE",FACE,{"disambiguationData":[OSD([sQuery(id+"F4.wireOp",EDGE,"E2.bottom")])]});var subQ2=makeQuery(id+"F3.boolean.opBoolean","COPY",FACE,{"derivedFrom":makeQuery(id+"F3.opExtrude","SWEPT_FACE",FACE,{"disambiguationData":[OSD([sQuery(id+"F2.wireOp",EDGE,"E1.bottom")])]})});var subQ3=sQuery(id+"F0.wireOp",EDGE,"E0.left");var subQ4=makeQuery(id+"F1.opExtrude","SWEPT_FACE",FACE,{"disambiguationData":[OSD([subQ3])]});var subQ14=makeQuery(id+"F5.boolean.opBoolean","MERGE",FACE,{"derivedFrom":[subQ2,subQ0]});var subQ16=sQuery(id+"F0.wireOp",EDGE,"E0.right");var subQ17=makeQuery(id+"F1.opExtrude","SWEPT_FACE",FACE,{"disambiguationData":[OSD([subQ16])]});var subQ21=sQuery(id+"F0.wireOp",EDGE,"E0.top");var subQ22=sQuery(id+"F0.wireOp",EDGE,"E0.bottom");Q6=makeQuery(id+"F11.boolean.opBoolean","INTERSECT",EDGE,{"derivedFrom":[makeQuery(id+"F9.opFillet","SPLIT",FACE,{"disambiguationData":[OD(0.0)],"derivedFrom":makeQuery(id+"F8.opFillet","MERGE",FACE,{"derivedFrom":[makeQuery(id+"F7.boolean.opBoolean","SPLIT",FACE,{"disambiguationData":[TD([makeQuery(id+"F1.opExtrude","CAP_FACE",FACE,{"disambiguationData":[OSD([subQ22,subQ21,subQ3,subQ16])],"isStart":false})])],"derivedFrom":subQ14}),makeQuery(id+"F7.boolean.opBoolean","SPLIT",FACE,{"disambiguationData":[TD([makeQuery(id+"F1.opExtrude","CAP_FACE",FACE,{"disambiguationData":[OSD([subQ22,subQ21,subQ3,subQ16])],"isStart":true})])],"derivedFrom":subQ14}),makeQuery(id+"F7.boolean.opBoolean","SPLIT",FACE,{"disambiguationData":[TD([subQ17])],"derivedFrom":subQ14}),makeQuery(id+"F7.boolean.opBoolean","SPLIT",FACE,{"disambiguationData":[TD([subQ4])],"derivedFrom":subQ14})]})}),makeQuery(id+"F11.opExtrude","SWEPT_FACE",FACE,{"disambiguationData":[OSD([sQuery(id+"F10.wireOp",EDGE,"E5.1.0.1")])]})]});}
            var Q7;
            {var subQ0=makeQuery(id+"F5.opExtrude","SWEPT_FACE",FACE,{"disambiguationData":[OSD([sQuery(id+"F4.wireOp",EDGE,"E2.bottom")])]});var subQ2=makeQuery(id+"F3.boolean.opBoolean","COPY",FACE,{"derivedFrom":makeQuery(id+"F3.opExtrude","SWEPT_FACE",FACE,{"disambiguationData":[OSD([sQuery(id+"F2.wireOp",EDGE,"E1.bottom")])]})});var subQ3=sQuery(id+"F0.wireOp",EDGE,"E0.left");var subQ4=makeQuery(id+"F1.opExtrude","SWEPT_FACE",FACE,{"disambiguationData":[OSD([subQ3])]});var subQ14=makeQuery(id+"F5.boolean.opBoolean","MERGE",FACE,{"derivedFrom":[subQ2,subQ0]});var subQ16=sQuery(id+"F0.wireOp",EDGE,"E0.right");var subQ17=makeQuery(id+"F1.opExtrude","SWEPT_FACE",FACE,{"disambiguationData":[OSD([subQ16])]});var subQ21=sQuery(id+"F0.wireOp",EDGE,"E0.top");var subQ22=sQuery(id+"F0.wireOp",EDGE,"E0.bottom");Q7=makeQuery(id+"F11.boolean.opBoolean","INTERSECT",EDGE,{"derivedFrom":[makeQuery(id+"F9.opFillet","SPLIT",FACE,{"disambiguationData":[OD(0.0)],"derivedFrom":makeQuery(id+"F8.opFillet","MERGE",FACE,{"derivedFrom":[makeQuery(id+"F7.boolean.opBoolean","SPLIT",FACE,{"disambiguationData":[TD([makeQuery(id+"F1.opExtrude","CAP_FACE",FACE,{"disambiguationData":[OSD([subQ22,subQ21,subQ3,subQ16])],"isStart":false})])],"derivedFrom":subQ14}),makeQuery(id+"F7.boolean.opBoolean","SPLIT",FACE,{"disambiguationData":[TD([makeQuery(id+"F1.opExtrude","CAP_FACE",FACE,{"disambiguationData":[OSD([subQ22,subQ21,subQ3,subQ16])],"isStart":true})])],"derivedFrom":subQ14}),makeQuery(id+"F7.boolean.opBoolean","SPLIT",FACE,{"disambiguationData":[TD([subQ17])],"derivedFrom":subQ14}),makeQuery(id+"F7.boolean.opBoolean","SPLIT",FACE,{"disambiguationData":[TD([subQ4])],"derivedFrom":subQ14})]})}),makeQuery(id+"F11.opExtrude","SWEPT_FACE",FACE,{"disambiguationData":[OSD([sQuery(id+"F10.wireOp",EDGE,"E5.2.0.1")])]})]});}
            var Q8;
            {var subQ0=makeQuery(id+"F5.opExtrude","SWEPT_FACE",FACE,{"disambiguationData":[OSD([sQuery(id+"F4.wireOp",EDGE,"E2.bottom")])]});var subQ2=makeQuery(id+"F3.boolean.opBoolean","COPY",FACE,{"derivedFrom":makeQuery(id+"F3.opExtrude","SWEPT_FACE",FACE,{"disambiguationData":[OSD([sQuery(id+"F2.wireOp",EDGE,"E1.bottom")])]})});var subQ3=sQuery(id+"F0.wireOp",EDGE,"E0.left");var subQ4=makeQuery(id+"F1.opExtrude","SWEPT_FACE",FACE,{"disambiguationData":[OSD([subQ3])]});var subQ14=makeQuery(id+"F5.boolean.opBoolean","MERGE",FACE,{"derivedFrom":[subQ2,subQ0]});var subQ16=sQuery(id+"F0.wireOp",EDGE,"E0.right");var subQ17=makeQuery(id+"F1.opExtrude","SWEPT_FACE",FACE,{"disambiguationData":[OSD([subQ16])]});var subQ21=sQuery(id+"F0.wireOp",EDGE,"E0.top");var subQ22=sQuery(id+"F0.wireOp",EDGE,"E0.bottom");Q8=makeQuery(id+"F11.boolean.opBoolean","INTERSECT",EDGE,{"derivedFrom":[makeQuery(id+"F9.opFillet","SPLIT",FACE,{"disambiguationData":[OD(1.0)],"derivedFrom":makeQuery(id+"F8.opFillet","MERGE",FACE,{"derivedFrom":[makeQuery(id+"F7.boolean.opBoolean","SPLIT",FACE,{"disambiguationData":[TD([makeQuery(id+"F1.opExtrude","CAP_FACE",FACE,{"disambiguationData":[OSD([subQ22,subQ21,subQ3,subQ16])],"isStart":false})])],"derivedFrom":subQ14}),makeQuery(id+"F7.boolean.opBoolean","SPLIT",FACE,{"disambiguationData":[TD([makeQuery(id+"F1.opExtrude","CAP_FACE",FACE,{"disambiguationData":[OSD([subQ22,subQ21,subQ3,subQ16])],"isStart":true})])],"derivedFrom":subQ14}),makeQuery(id+"F7.boolean.opBoolean","SPLIT",FACE,{"disambiguationData":[TD([subQ17])],"derivedFrom":subQ14}),makeQuery(id+"F7.boolean.opBoolean","SPLIT",FACE,{"disambiguationData":[TD([subQ4])],"derivedFrom":subQ14})]})}),makeQuery(id+"F11.opExtrude","SWEPT_FACE",FACE,{"disambiguationData":[OSD([sQuery(id+"F10.wireOp",EDGE,"E6.0.1.9")])]})]});}
            var Q9;
            {var subQ0=makeQuery(id+"F5.opExtrude","SWEPT_FACE",FACE,{"disambiguationData":[OSD([sQuery(id+"F4.wireOp",EDGE,"E2.bottom")])]});var subQ2=makeQuery(id+"F3.boolean.opBoolean","COPY",FACE,{"derivedFrom":makeQuery(id+"F3.opExtrude","SWEPT_FACE",FACE,{"disambiguationData":[OSD([sQuery(id+"F2.wireOp",EDGE,"E1.bottom")])]})});var subQ3=sQuery(id+"F0.wireOp",EDGE,"E0.left");var subQ4=makeQuery(id+"F1.opExtrude","SWEPT_FACE",FACE,{"disambiguationData":[OSD([subQ3])]});var subQ14=makeQuery(id+"F5.boolean.opBoolean","MERGE",FACE,{"derivedFrom":[subQ2,subQ0]});var subQ16=sQuery(id+"F0.wireOp",EDGE,"E0.right");var subQ17=makeQuery(id+"F1.opExtrude","SWEPT_FACE",FACE,{"disambiguationData":[OSD([subQ16])]});var subQ21=sQuery(id+"F0.wireOp",EDGE,"E0.top");var subQ22=sQuery(id+"F0.wireOp",EDGE,"E0.bottom");Q9=makeQuery(id+"F11.boolean.opBoolean","INTERSECT",EDGE,{"derivedFrom":[makeQuery(id+"F9.opFillet","SPLIT",FACE,{"disambiguationData":[OD(1.0)],"derivedFrom":makeQuery(id+"F8.opFillet","MERGE",FACE,{"derivedFrom":[makeQuery(id+"F7.boolean.opBoolean","SPLIT",FACE,{"disambiguationData":[TD([makeQuery(id+"F1.opExtrude","CAP_FACE",FACE,{"disambiguationData":[OSD([subQ22,subQ21,subQ3,subQ16])],"isStart":false})])],"derivedFrom":subQ14}),makeQuery(id+"F7.boolean.opBoolean","SPLIT",FACE,{"disambiguationData":[TD([makeQuery(id+"F1.opExtrude","CAP_FACE",FACE,{"disambiguationData":[OSD([subQ22,subQ21,subQ3,subQ16])],"isStart":true})])],"derivedFrom":subQ14}),makeQuery(id+"F7.boolean.opBoolean","SPLIT",FACE,{"disambiguationData":[TD([subQ17])],"derivedFrom":subQ14}),makeQuery(id+"F7.boolean.opBoolean","SPLIT",FACE,{"disambiguationData":[TD([subQ4])],"derivedFrom":subQ14})]})}),makeQuery(id+"F11.opExtrude","SWEPT_FACE",FACE,{"disambiguationData":[OSD([sQuery(id+"F10.wireOp",EDGE,"E6.0.1.7")])]})]});}
            var Q10;
            {var subQ0=makeQuery(id+"F5.opExtrude","SWEPT_FACE",FACE,{"disambiguationData":[OSD([sQuery(id+"F4.wireOp",EDGE,"E2.bottom")])]});var subQ2=makeQuery(id+"F3.boolean.opBoolean","COPY",FACE,{"derivedFrom":makeQuery(id+"F3.opExtrude","SWEPT_FACE",FACE,{"disambiguationData":[OSD([sQuery(id+"F2.wireOp",EDGE,"E1.bottom")])]})});var subQ3=sQuery(id+"F0.wireOp",EDGE,"E0.left");var subQ4=makeQuery(id+"F1.opExtrude","SWEPT_FACE",FACE,{"disambiguationData":[OSD([subQ3])]});var subQ14=makeQuery(id+"F5.boolean.opBoolean","MERGE",FACE,{"derivedFrom":[subQ2,subQ0]});var subQ16=sQuery(id+"F0.wireOp",EDGE,"E0.right");var subQ17=makeQuery(id+"F1.opExtrude","SWEPT_FACE",FACE,{"disambiguationData":[OSD([subQ16])]});var subQ21=sQuery(id+"F0.wireOp",EDGE,"E0.top");var subQ22=sQuery(id+"F0.wireOp",EDGE,"E0.bottom");Q10=makeQuery(id+"F11.boolean.opBoolean","INTERSECT",EDGE,{"derivedFrom":[makeQuery(id+"F9.opFillet","SPLIT",FACE,{"disambiguationData":[OD(2.0)],"derivedFrom":makeQuery(id+"F8.opFillet","MERGE",FACE,{"derivedFrom":[makeQuery(id+"F7.boolean.opBoolean","SPLIT",FACE,{"disambiguationData":[TD([makeQuery(id+"F1.opExtrude","CAP_FACE",FACE,{"disambiguationData":[OSD([subQ22,subQ21,subQ3,subQ16])],"isStart":false})])],"derivedFrom":subQ14}),makeQuery(id+"F7.boolean.opBoolean","SPLIT",FACE,{"disambiguationData":[TD([makeQuery(id+"F1.opExtrude","CAP_FACE",FACE,{"disambiguationData":[OSD([subQ22,subQ21,subQ3,subQ16])],"isStart":true})])],"derivedFrom":subQ14}),makeQuery(id+"F7.boolean.opBoolean","SPLIT",FACE,{"disambiguationData":[TD([subQ17])],"derivedFrom":subQ14}),makeQuery(id+"F7.boolean.opBoolean","SPLIT",FACE,{"disambiguationData":[TD([subQ4])],"derivedFrom":subQ14})]})}),makeQuery(id+"F11.opExtrude","SWEPT_FACE",FACE,{"disambiguationData":[OSD([sQuery(id+"F10.wireOp",EDGE,"E8.0.2.1")])]})]});}
            var Q11;
            {var subQ0=makeQuery(id+"F5.opExtrude","SWEPT_FACE",FACE,{"disambiguationData":[OSD([sQuery(id+"F4.wireOp",EDGE,"E2.bottom")])]});var subQ2=makeQuery(id+"F3.boolean.opBoolean","COPY",FACE,{"derivedFrom":makeQuery(id+"F3.opExtrude","SWEPT_FACE",FACE,{"disambiguationData":[OSD([sQuery(id+"F2.wireOp",EDGE,"E1.bottom")])]})});var subQ3=sQuery(id+"F0.wireOp",EDGE,"E0.left");var subQ4=makeQuery(id+"F1.opExtrude","SWEPT_FACE",FACE,{"disambiguationData":[OSD([subQ3])]});var subQ14=makeQuery(id+"F5.boolean.opBoolean","MERGE",FACE,{"derivedFrom":[subQ2,subQ0]});var subQ16=sQuery(id+"F0.wireOp",EDGE,"E0.right");var subQ17=makeQuery(id+"F1.opExtrude","SWEPT_FACE",FACE,{"disambiguationData":[OSD([subQ16])]});var subQ21=sQuery(id+"F0.wireOp",EDGE,"E0.top");var subQ22=sQuery(id+"F0.wireOp",EDGE,"E0.bottom");Q11=makeQuery(id+"F11.boolean.opBoolean","INTERSECT",EDGE,{"derivedFrom":[makeQuery(id+"F9.opFillet","SPLIT",FACE,{"disambiguationData":[OD(2.0)],"derivedFrom":makeQuery(id+"F8.opFillet","MERGE",FACE,{"derivedFrom":[makeQuery(id+"F7.boolean.opBoolean","SPLIT",FACE,{"disambiguationData":[TD([makeQuery(id+"F1.opExtrude","CAP_FACE",FACE,{"disambiguationData":[OSD([subQ22,subQ21,subQ3,subQ16])],"isStart":false})])],"derivedFrom":subQ14}),makeQuery(id+"F7.boolean.opBoolean","SPLIT",FACE,{"disambiguationData":[TD([makeQuery(id+"F1.opExtrude","CAP_FACE",FACE,{"disambiguationData":[OSD([subQ22,subQ21,subQ3,subQ16])],"isStart":true})])],"derivedFrom":subQ14}),makeQuery(id+"F7.boolean.opBoolean","SPLIT",FACE,{"disambiguationData":[TD([subQ17])],"derivedFrom":subQ14}),makeQuery(id+"F7.boolean.opBoolean","SPLIT",FACE,{"disambiguationData":[TD([subQ4])],"derivedFrom":subQ14})]})}),makeQuery(id+"F11.opExtrude","SWEPT_FACE",FACE,{"disambiguationData":[OSD([sQuery(id+"F10.wireOp",EDGE,"E8.0.1.1")])]})]});}
            var Q12;
            {var subQ0=makeQuery(id+"F5.opExtrude","SWEPT_FACE",FACE,{"disambiguationData":[OSD([sQuery(id+"F4.wireOp",EDGE,"E2.bottom")])]});var subQ2=makeQuery(id+"F3.boolean.opBoolean","COPY",FACE,{"derivedFrom":makeQuery(id+"F3.opExtrude","SWEPT_FACE",FACE,{"disambiguationData":[OSD([sQuery(id+"F2.wireOp",EDGE,"E1.bottom")])]})});var subQ3=sQuery(id+"F0.wireOp",EDGE,"E0.left");var subQ4=makeQuery(id+"F1.opExtrude","SWEPT_FACE",FACE,{"disambiguationData":[OSD([subQ3])]});var subQ14=makeQuery(id+"F5.boolean.opBoolean","MERGE",FACE,{"derivedFrom":[subQ2,subQ0]});var subQ16=sQuery(id+"F0.wireOp",EDGE,"E0.right");var subQ17=makeQuery(id+"F1.opExtrude","SWEPT_FACE",FACE,{"disambiguationData":[OSD([subQ16])]});var subQ21=sQuery(id+"F0.wireOp",EDGE,"E0.top");var subQ22=sQuery(id+"F0.wireOp",EDGE,"E0.bottom");Q12=makeQuery(id+"F11.boolean.opBoolean","INTERSECT",EDGE,{"derivedFrom":[makeQuery(id+"F9.opFillet","SPLIT",FACE,{"disambiguationData":[OD(2.0)],"derivedFrom":makeQuery(id+"F8.opFillet","MERGE",FACE,{"derivedFrom":[makeQuery(id+"F7.boolean.opBoolean","SPLIT",FACE,{"disambiguationData":[TD([makeQuery(id+"F1.opExtrude","CAP_FACE",FACE,{"disambiguationData":[OSD([subQ22,subQ21,subQ3,subQ16])],"isStart":false})])],"derivedFrom":subQ14}),makeQuery(id+"F7.boolean.opBoolean","SPLIT",FACE,{"disambiguationData":[TD([makeQuery(id+"F1.opExtrude","CAP_FACE",FACE,{"disambiguationData":[OSD([subQ22,subQ21,subQ3,subQ16])],"isStart":true})])],"derivedFrom":subQ14}),makeQuery(id+"F7.boolean.opBoolean","SPLIT",FACE,{"disambiguationData":[TD([subQ17])],"derivedFrom":subQ14}),makeQuery(id+"F7.boolean.opBoolean","SPLIT",FACE,{"disambiguationData":[TD([subQ4])],"derivedFrom":subQ14})]})}),makeQuery(id+"F11.opExtrude","SWEPT_FACE",FACE,{"disambiguationData":[OSD([sQuery(id+"F10.wireOp",EDGE,"E7.bottom")])]})]});}
            var Q13;
            {var subQ1=makeQuery(id+"F5.opExtrude","SWEPT_FACE",FACE,{"disambiguationData":[OSD([sQuery(id+"F4.wireOp",EDGE,"E2.top")])]});var subQ2=makeQuery(id+"F3.boolean.opBoolean","COPY",FACE,{"derivedFrom":makeQuery(id+"F3.opExtrude","SWEPT_FACE",FACE,{"disambiguationData":[OSD([sQuery(id+"F2.wireOp",EDGE,"E1.top")])]})});var subQ3=sQuery(id+"F0.wireOp",EDGE,"E0.left");var subQ4=makeQuery(id+"F1.opExtrude","SWEPT_FACE",FACE,{"disambiguationData":[OSD([subQ3])]});var subQ14=makeQuery(id+"F5.boolean.opBoolean","MERGE",FACE,{"derivedFrom":[subQ2,subQ1]});var subQ16=sQuery(id+"F0.wireOp",EDGE,"E0.right");var subQ17=makeQuery(id+"F1.opExtrude","SWEPT_FACE",FACE,{"disambiguationData":[OSD([subQ16])]});var subQ21=sQuery(id+"F0.wireOp",EDGE,"E0.top");var subQ22=sQuery(id+"F0.wireOp",EDGE,"E0.bottom");Q13=makeQuery(id+"F11.boolean.opBoolean","INTERSECT",EDGE,{"derivedFrom":[makeQuery(id+"F9.opFillet","SPLIT",FACE,{"disambiguationData":[OD(2.0)],"derivedFrom":makeQuery(id+"F8.opFillet","MERGE",FACE,{"derivedFrom":[makeQuery(id+"F7.boolean.opBoolean","SPLIT",FACE,{"disambiguationData":[TD([makeQuery(id+"F1.opExtrude","CAP_FACE",FACE,{"disambiguationData":[OSD([subQ22,subQ21,subQ3,subQ16])],"isStart":false})])],"derivedFrom":subQ14}),makeQuery(id+"F7.boolean.opBoolean","SPLIT",FACE,{"disambiguationData":[TD([makeQuery(id+"F1.opExtrude","CAP_FACE",FACE,{"disambiguationData":[OSD([subQ22,subQ21,subQ3,subQ16])],"isStart":true})])],"derivedFrom":subQ14}),makeQuery(id+"F7.boolean.opBoolean","SPLIT",FACE,{"disambiguationData":[TD([subQ17])],"derivedFrom":subQ14}),makeQuery(id+"F7.boolean.opBoolean","SPLIT",FACE,{"disambiguationData":[TD([subQ4])],"derivedFrom":subQ14})]})}),makeQuery(id+"F11.opExtrude","SWEPT_FACE",FACE,{"disambiguationData":[OSD([sQuery(id+"F10.wireOp",EDGE,"E7.bottom")])]})]});}
            var Q14;
            {var subQ1=makeQuery(id+"F5.opExtrude","SWEPT_FACE",FACE,{"disambiguationData":[OSD([sQuery(id+"F4.wireOp",EDGE,"E2.top")])]});var subQ2=makeQuery(id+"F3.boolean.opBoolean","COPY",FACE,{"derivedFrom":makeQuery(id+"F3.opExtrude","SWEPT_FACE",FACE,{"disambiguationData":[OSD([sQuery(id+"F2.wireOp",EDGE,"E1.top")])]})});var subQ3=sQuery(id+"F0.wireOp",EDGE,"E0.left");var subQ4=makeQuery(id+"F1.opExtrude","SWEPT_FACE",FACE,{"disambiguationData":[OSD([subQ3])]});var subQ14=makeQuery(id+"F5.boolean.opBoolean","MERGE",FACE,{"derivedFrom":[subQ2,subQ1]});var subQ16=sQuery(id+"F0.wireOp",EDGE,"E0.right");var subQ17=makeQuery(id+"F1.opExtrude","SWEPT_FACE",FACE,{"disambiguationData":[OSD([subQ16])]});var subQ21=sQuery(id+"F0.wireOp",EDGE,"E0.top");var subQ22=sQuery(id+"F0.wireOp",EDGE,"E0.bottom");Q14=makeQuery(id+"F11.boolean.opBoolean","INTERSECT",EDGE,{"derivedFrom":[makeQuery(id+"F9.opFillet","SPLIT",FACE,{"disambiguationData":[OD(2.0)],"derivedFrom":makeQuery(id+"F8.opFillet","MERGE",FACE,{"derivedFrom":[makeQuery(id+"F7.boolean.opBoolean","SPLIT",FACE,{"disambiguationData":[TD([makeQuery(id+"F1.opExtrude","CAP_FACE",FACE,{"disambiguationData":[OSD([subQ22,subQ21,subQ3,subQ16])],"isStart":false})])],"derivedFrom":subQ14}),makeQuery(id+"F7.boolean.opBoolean","SPLIT",FACE,{"disambiguationData":[TD([makeQuery(id+"F1.opExtrude","CAP_FACE",FACE,{"disambiguationData":[OSD([subQ22,subQ21,subQ3,subQ16])],"isStart":true})])],"derivedFrom":subQ14}),makeQuery(id+"F7.boolean.opBoolean","SPLIT",FACE,{"disambiguationData":[TD([subQ17])],"derivedFrom":subQ14}),makeQuery(id+"F7.boolean.opBoolean","SPLIT",FACE,{"disambiguationData":[TD([subQ4])],"derivedFrom":subQ14})]})}),makeQuery(id+"F11.opExtrude","SWEPT_FACE",FACE,{"disambiguationData":[OSD([sQuery(id+"F10.wireOp",EDGE,"E8.0.1.1")])]})]});}
            var Q15;
            {var subQ1=makeQuery(id+"F5.opExtrude","SWEPT_FACE",FACE,{"disambiguationData":[OSD([sQuery(id+"F4.wireOp",EDGE,"E2.top")])]});var subQ2=makeQuery(id+"F3.boolean.opBoolean","COPY",FACE,{"derivedFrom":makeQuery(id+"F3.opExtrude","SWEPT_FACE",FACE,{"disambiguationData":[OSD([sQuery(id+"F2.wireOp",EDGE,"E1.top")])]})});var subQ3=sQuery(id+"F0.wireOp",EDGE,"E0.left");var subQ4=makeQuery(id+"F1.opExtrude","SWEPT_FACE",FACE,{"disambiguationData":[OSD([subQ3])]});var subQ14=makeQuery(id+"F5.boolean.opBoolean","MERGE",FACE,{"derivedFrom":[subQ2,subQ1]});var subQ16=sQuery(id+"F0.wireOp",EDGE,"E0.right");var subQ17=makeQuery(id+"F1.opExtrude","SWEPT_FACE",FACE,{"disambiguationData":[OSD([subQ16])]});var subQ21=sQuery(id+"F0.wireOp",EDGE,"E0.top");var subQ22=sQuery(id+"F0.wireOp",EDGE,"E0.bottom");Q15=makeQuery(id+"F11.boolean.opBoolean","INTERSECT",EDGE,{"derivedFrom":[makeQuery(id+"F9.opFillet","SPLIT",FACE,{"disambiguationData":[OD(2.0)],"derivedFrom":makeQuery(id+"F8.opFillet","MERGE",FACE,{"derivedFrom":[makeQuery(id+"F7.boolean.opBoolean","SPLIT",FACE,{"disambiguationData":[TD([makeQuery(id+"F1.opExtrude","CAP_FACE",FACE,{"disambiguationData":[OSD([subQ22,subQ21,subQ3,subQ16])],"isStart":false})])],"derivedFrom":subQ14}),makeQuery(id+"F7.boolean.opBoolean","SPLIT",FACE,{"disambiguationData":[TD([makeQuery(id+"F1.opExtrude","CAP_FACE",FACE,{"disambiguationData":[OSD([subQ22,subQ21,subQ3,subQ16])],"isStart":true})])],"derivedFrom":subQ14}),makeQuery(id+"F7.boolean.opBoolean","SPLIT",FACE,{"disambiguationData":[TD([subQ17])],"derivedFrom":subQ14}),makeQuery(id+"F7.boolean.opBoolean","SPLIT",FACE,{"disambiguationData":[TD([subQ4])],"derivedFrom":subQ14})]})}),makeQuery(id+"F11.opExtrude","SWEPT_FACE",FACE,{"disambiguationData":[OSD([sQuery(id+"F10.wireOp",EDGE,"E8.0.2.1")])]})]});}
            var Q16;
            {var subQ0=makeQuery(id+"F5.opExtrude","SWEPT_FACE",FACE,{"disambiguationData":[OSD([sQuery(id+"F4.wireOp",EDGE,"E2.bottom")])]});var subQ2=makeQuery(id+"F3.boolean.opBoolean","COPY",FACE,{"derivedFrom":makeQuery(id+"F3.opExtrude","SWEPT_FACE",FACE,{"disambiguationData":[OSD([sQuery(id+"F2.wireOp",EDGE,"E1.bottom")])]})});var subQ3=sQuery(id+"F0.wireOp",EDGE,"E0.left");var subQ4=makeQuery(id+"F1.opExtrude","SWEPT_FACE",FACE,{"disambiguationData":[OSD([subQ3])]});var subQ14=makeQuery(id+"F5.boolean.opBoolean","MERGE",FACE,{"derivedFrom":[subQ2,subQ0]});var subQ16=sQuery(id+"F0.wireOp",EDGE,"E0.right");var subQ17=makeQuery(id+"F1.opExtrude","SWEPT_FACE",FACE,{"disambiguationData":[OSD([subQ16])]});var subQ21=sQuery(id+"F0.wireOp",EDGE,"E0.top");var subQ22=sQuery(id+"F0.wireOp",EDGE,"E0.bottom");Q16=makeQuery(id+"F11.boolean.opBoolean","INTERSECT",EDGE,{"derivedFrom":[makeQuery(id+"F9.opFillet","SPLIT",FACE,{"disambiguationData":[OD(0.0)],"derivedFrom":makeQuery(id+"F8.opFillet","MERGE",FACE,{"derivedFrom":[makeQuery(id+"F7.boolean.opBoolean","SPLIT",FACE,{"disambiguationData":[TD([makeQuery(id+"F1.opExtrude","CAP_FACE",FACE,{"disambiguationData":[OSD([subQ22,subQ21,subQ3,subQ16])],"isStart":false})])],"derivedFrom":subQ14}),makeQuery(id+"F7.boolean.opBoolean","SPLIT",FACE,{"disambiguationData":[TD([makeQuery(id+"F1.opExtrude","CAP_FACE",FACE,{"disambiguationData":[OSD([subQ22,subQ21,subQ3,subQ16])],"isStart":true})])],"derivedFrom":subQ14}),makeQuery(id+"F7.boolean.opBoolean","SPLIT",FACE,{"disambiguationData":[TD([subQ17])],"derivedFrom":subQ14}),makeQuery(id+"F7.boolean.opBoolean","SPLIT",FACE,{"disambiguationData":[TD([subQ4])],"derivedFrom":subQ14})]})}),makeQuery(id+"F11.opExtrude","SWEPT_FACE",FACE,{"disambiguationData":[OSD([sQuery(id+"F10.wireOp",EDGE,"E4.left")])]})]});}
            var Q17;
            {var subQ0=makeQuery(id+"F5.opExtrude","SWEPT_FACE",FACE,{"disambiguationData":[OSD([sQuery(id+"F4.wireOp",EDGE,"E2.bottom")])]});var subQ2=makeQuery(id+"F3.boolean.opBoolean","COPY",FACE,{"derivedFrom":makeQuery(id+"F3.opExtrude","SWEPT_FACE",FACE,{"disambiguationData":[OSD([sQuery(id+"F2.wireOp",EDGE,"E1.bottom")])]})});var subQ3=sQuery(id+"F0.wireOp",EDGE,"E0.left");var subQ4=makeQuery(id+"F1.opExtrude","SWEPT_FACE",FACE,{"disambiguationData":[OSD([subQ3])]});var subQ14=makeQuery(id+"F5.boolean.opBoolean","MERGE",FACE,{"derivedFrom":[subQ2,subQ0]});var subQ16=sQuery(id+"F0.wireOp",EDGE,"E0.right");var subQ17=makeQuery(id+"F1.opExtrude","SWEPT_FACE",FACE,{"disambiguationData":[OSD([subQ16])]});var subQ21=sQuery(id+"F0.wireOp",EDGE,"E0.top");var subQ22=sQuery(id+"F0.wireOp",EDGE,"E0.bottom");Q17=makeQuery(id+"F11.boolean.opBoolean","INTERSECT",EDGE,{"derivedFrom":[makeQuery(id+"F9.opFillet","SPLIT",FACE,{"disambiguationData":[OD(0.0)],"derivedFrom":makeQuery(id+"F8.opFillet","MERGE",FACE,{"derivedFrom":[makeQuery(id+"F7.boolean.opBoolean","SPLIT",FACE,{"disambiguationData":[TD([makeQuery(id+"F1.opExtrude","CAP_FACE",FACE,{"disambiguationData":[OSD([subQ22,subQ21,subQ3,subQ16])],"isStart":false})])],"derivedFrom":subQ14}),makeQuery(id+"F7.boolean.opBoolean","SPLIT",FACE,{"disambiguationData":[TD([makeQuery(id+"F1.opExtrude","CAP_FACE",FACE,{"disambiguationData":[OSD([subQ22,subQ21,subQ3,subQ16])],"isStart":true})])],"derivedFrom":subQ14}),makeQuery(id+"F7.boolean.opBoolean","SPLIT",FACE,{"disambiguationData":[TD([subQ17])],"derivedFrom":subQ14}),makeQuery(id+"F7.boolean.opBoolean","SPLIT",FACE,{"disambiguationData":[TD([subQ4])],"derivedFrom":subQ14})]})}),makeQuery(id+"F11.opExtrude","SWEPT_FACE",FACE,{"disambiguationData":[OSD([sQuery(id+"F10.wireOp",EDGE,"E5.1.0.0")])]})]});}
            var Q18;
            {var subQ0=makeQuery(id+"F5.opExtrude","SWEPT_FACE",FACE,{"disambiguationData":[OSD([sQuery(id+"F4.wireOp",EDGE,"E2.bottom")])]});var subQ2=makeQuery(id+"F3.boolean.opBoolean","COPY",FACE,{"derivedFrom":makeQuery(id+"F3.opExtrude","SWEPT_FACE",FACE,{"disambiguationData":[OSD([sQuery(id+"F2.wireOp",EDGE,"E1.bottom")])]})});var subQ3=sQuery(id+"F0.wireOp",EDGE,"E0.left");var subQ4=makeQuery(id+"F1.opExtrude","SWEPT_FACE",FACE,{"disambiguationData":[OSD([subQ3])]});var subQ14=makeQuery(id+"F5.boolean.opBoolean","MERGE",FACE,{"derivedFrom":[subQ2,subQ0]});var subQ16=sQuery(id+"F0.wireOp",EDGE,"E0.right");var subQ17=makeQuery(id+"F1.opExtrude","SWEPT_FACE",FACE,{"disambiguationData":[OSD([subQ16])]});var subQ21=sQuery(id+"F0.wireOp",EDGE,"E0.top");var subQ22=sQuery(id+"F0.wireOp",EDGE,"E0.bottom");Q18=makeQuery(id+"F11.boolean.opBoolean","INTERSECT",EDGE,{"derivedFrom":[makeQuery(id+"F9.opFillet","SPLIT",FACE,{"disambiguationData":[OD(0.0)],"derivedFrom":makeQuery(id+"F8.opFillet","MERGE",FACE,{"derivedFrom":[makeQuery(id+"F7.boolean.opBoolean","SPLIT",FACE,{"disambiguationData":[TD([makeQuery(id+"F1.opExtrude","CAP_FACE",FACE,{"disambiguationData":[OSD([subQ22,subQ21,subQ3,subQ16])],"isStart":false})])],"derivedFrom":subQ14}),makeQuery(id+"F7.boolean.opBoolean","SPLIT",FACE,{"disambiguationData":[TD([makeQuery(id+"F1.opExtrude","CAP_FACE",FACE,{"disambiguationData":[OSD([subQ22,subQ21,subQ3,subQ16])],"isStart":true})])],"derivedFrom":subQ14}),makeQuery(id+"F7.boolean.opBoolean","SPLIT",FACE,{"disambiguationData":[TD([subQ17])],"derivedFrom":subQ14}),makeQuery(id+"F7.boolean.opBoolean","SPLIT",FACE,{"disambiguationData":[TD([subQ4])],"derivedFrom":subQ14})]})}),makeQuery(id+"F11.opExtrude","SWEPT_FACE",FACE,{"disambiguationData":[OSD([sQuery(id+"F10.wireOp",EDGE,"E5.2.0.0")])]})]});}
            var Q19;
            {var subQ1=makeQuery(id+"F5.opExtrude","SWEPT_FACE",FACE,{"disambiguationData":[OSD([sQuery(id+"F4.wireOp",EDGE,"E2.top")])]});var subQ2=makeQuery(id+"F3.boolean.opBoolean","COPY",FACE,{"derivedFrom":makeQuery(id+"F3.opExtrude","SWEPT_FACE",FACE,{"disambiguationData":[OSD([sQuery(id+"F2.wireOp",EDGE,"E1.top")])]})});var subQ3=sQuery(id+"F0.wireOp",EDGE,"E0.left");var subQ4=makeQuery(id+"F1.opExtrude","SWEPT_FACE",FACE,{"disambiguationData":[OSD([subQ3])]});var subQ14=makeQuery(id+"F5.boolean.opBoolean","MERGE",FACE,{"derivedFrom":[subQ2,subQ1]});var subQ16=sQuery(id+"F0.wireOp",EDGE,"E0.right");var subQ17=makeQuery(id+"F1.opExtrude","SWEPT_FACE",FACE,{"disambiguationData":[OSD([subQ16])]});var subQ21=sQuery(id+"F0.wireOp",EDGE,"E0.top");var subQ22=sQuery(id+"F0.wireOp",EDGE,"E0.bottom");Q19=makeQuery(id+"F11.boolean.opBoolean","INTERSECT",EDGE,{"derivedFrom":[makeQuery(id+"F9.opFillet","SPLIT",FACE,{"disambiguationData":[OD(0.0)],"derivedFrom":makeQuery(id+"F8.opFillet","MERGE",FACE,{"derivedFrom":[makeQuery(id+"F7.boolean.opBoolean","SPLIT",FACE,{"disambiguationData":[TD([makeQuery(id+"F1.opExtrude","CAP_FACE",FACE,{"disambiguationData":[OSD([subQ22,subQ21,subQ3,subQ16])],"isStart":false})])],"derivedFrom":subQ14}),makeQuery(id+"F7.boolean.opBoolean","SPLIT",FACE,{"disambiguationData":[TD([makeQuery(id+"F1.opExtrude","CAP_FACE",FACE,{"disambiguationData":[OSD([subQ22,subQ21,subQ3,subQ16])],"isStart":true})])],"derivedFrom":subQ14}),makeQuery(id+"F7.boolean.opBoolean","SPLIT",FACE,{"disambiguationData":[TD([subQ17])],"derivedFrom":subQ14}),makeQuery(id+"F7.boolean.opBoolean","SPLIT",FACE,{"disambiguationData":[TD([subQ4])],"derivedFrom":subQ14})]})}),makeQuery(id+"F11.opExtrude","SWEPT_FACE",FACE,{"disambiguationData":[OSD([sQuery(id+"F10.wireOp",EDGE,"E5.2.0.0")])]})]});}
            var Q20;
            {var subQ1=makeQuery(id+"F5.opExtrude","SWEPT_FACE",FACE,{"disambiguationData":[OSD([sQuery(id+"F4.wireOp",EDGE,"E2.top")])]});var subQ2=makeQuery(id+"F3.boolean.opBoolean","COPY",FACE,{"derivedFrom":makeQuery(id+"F3.opExtrude","SWEPT_FACE",FACE,{"disambiguationData":[OSD([sQuery(id+"F2.wireOp",EDGE,"E1.top")])]})});var subQ3=sQuery(id+"F0.wireOp",EDGE,"E0.left");var subQ4=makeQuery(id+"F1.opExtrude","SWEPT_FACE",FACE,{"disambiguationData":[OSD([subQ3])]});var subQ14=makeQuery(id+"F5.boolean.opBoolean","MERGE",FACE,{"derivedFrom":[subQ2,subQ1]});var subQ16=sQuery(id+"F0.wireOp",EDGE,"E0.right");var subQ17=makeQuery(id+"F1.opExtrude","SWEPT_FACE",FACE,{"disambiguationData":[OSD([subQ16])]});var subQ21=sQuery(id+"F0.wireOp",EDGE,"E0.top");var subQ22=sQuery(id+"F0.wireOp",EDGE,"E0.bottom");Q20=makeQuery(id+"F11.boolean.opBoolean","INTERSECT",EDGE,{"derivedFrom":[makeQuery(id+"F9.opFillet","SPLIT",FACE,{"disambiguationData":[OD(0.0)],"derivedFrom":makeQuery(id+"F8.opFillet","MERGE",FACE,{"derivedFrom":[makeQuery(id+"F7.boolean.opBoolean","SPLIT",FACE,{"disambiguationData":[TD([makeQuery(id+"F1.opExtrude","CAP_FACE",FACE,{"disambiguationData":[OSD([subQ22,subQ21,subQ3,subQ16])],"isStart":false})])],"derivedFrom":subQ14}),makeQuery(id+"F7.boolean.opBoolean","SPLIT",FACE,{"disambiguationData":[TD([makeQuery(id+"F1.opExtrude","CAP_FACE",FACE,{"disambiguationData":[OSD([subQ22,subQ21,subQ3,subQ16])],"isStart":true})])],"derivedFrom":subQ14}),makeQuery(id+"F7.boolean.opBoolean","SPLIT",FACE,{"disambiguationData":[TD([subQ17])],"derivedFrom":subQ14}),makeQuery(id+"F7.boolean.opBoolean","SPLIT",FACE,{"disambiguationData":[TD([subQ4])],"derivedFrom":subQ14})]})}),makeQuery(id+"F11.opExtrude","SWEPT_FACE",FACE,{"disambiguationData":[OSD([sQuery(id+"F10.wireOp",EDGE,"E5.1.0.0")])]})]});}
            var Q21;
            {var subQ1=makeQuery(id+"F5.opExtrude","SWEPT_FACE",FACE,{"disambiguationData":[OSD([sQuery(id+"F4.wireOp",EDGE,"E2.top")])]});var subQ2=makeQuery(id+"F3.boolean.opBoolean","COPY",FACE,{"derivedFrom":makeQuery(id+"F3.opExtrude","SWEPT_FACE",FACE,{"disambiguationData":[OSD([sQuery(id+"F2.wireOp",EDGE,"E1.top")])]})});var subQ3=sQuery(id+"F0.wireOp",EDGE,"E0.left");var subQ4=makeQuery(id+"F1.opExtrude","SWEPT_FACE",FACE,{"disambiguationData":[OSD([subQ3])]});var subQ14=makeQuery(id+"F5.boolean.opBoolean","MERGE",FACE,{"derivedFrom":[subQ2,subQ1]});var subQ16=sQuery(id+"F0.wireOp",EDGE,"E0.right");var subQ17=makeQuery(id+"F1.opExtrude","SWEPT_FACE",FACE,{"disambiguationData":[OSD([subQ16])]});var subQ21=sQuery(id+"F0.wireOp",EDGE,"E0.top");var subQ22=sQuery(id+"F0.wireOp",EDGE,"E0.bottom");Q21=makeQuery(id+"F11.boolean.opBoolean","INTERSECT",EDGE,{"derivedFrom":[makeQuery(id+"F9.opFillet","SPLIT",FACE,{"disambiguationData":[OD(0.0)],"derivedFrom":makeQuery(id+"F8.opFillet","MERGE",FACE,{"derivedFrom":[makeQuery(id+"F7.boolean.opBoolean","SPLIT",FACE,{"disambiguationData":[TD([makeQuery(id+"F1.opExtrude","CAP_FACE",FACE,{"disambiguationData":[OSD([subQ22,subQ21,subQ3,subQ16])],"isStart":false})])],"derivedFrom":subQ14}),makeQuery(id+"F7.boolean.opBoolean","SPLIT",FACE,{"disambiguationData":[TD([makeQuery(id+"F1.opExtrude","CAP_FACE",FACE,{"disambiguationData":[OSD([subQ22,subQ21,subQ3,subQ16])],"isStart":true})])],"derivedFrom":subQ14}),makeQuery(id+"F7.boolean.opBoolean","SPLIT",FACE,{"disambiguationData":[TD([subQ17])],"derivedFrom":subQ14}),makeQuery(id+"F7.boolean.opBoolean","SPLIT",FACE,{"disambiguationData":[TD([subQ4])],"derivedFrom":subQ14})]})}),makeQuery(id+"F11.opExtrude","SWEPT_FACE",FACE,{"disambiguationData":[OSD([sQuery(id+"F10.wireOp",EDGE,"E4.left")])]})]});}
            var Q22;
            {var subQ1=makeQuery(id+"F5.opExtrude","SWEPT_FACE",FACE,{"disambiguationData":[OSD([sQuery(id+"F4.wireOp",EDGE,"E2.top")])]});var subQ2=makeQuery(id+"F3.boolean.opBoolean","COPY",FACE,{"derivedFrom":makeQuery(id+"F3.opExtrude","SWEPT_FACE",FACE,{"disambiguationData":[OSD([sQuery(id+"F2.wireOp",EDGE,"E1.top")])]})});var subQ3=sQuery(id+"F0.wireOp",EDGE,"E0.left");var subQ4=makeQuery(id+"F1.opExtrude","SWEPT_FACE",FACE,{"disambiguationData":[OSD([subQ3])]});var subQ14=makeQuery(id+"F5.boolean.opBoolean","MERGE",FACE,{"derivedFrom":[subQ2,subQ1]});var subQ16=sQuery(id+"F0.wireOp",EDGE,"E0.right");var subQ17=makeQuery(id+"F1.opExtrude","SWEPT_FACE",FACE,{"disambiguationData":[OSD([subQ16])]});var subQ21=sQuery(id+"F0.wireOp",EDGE,"E0.top");var subQ22=sQuery(id+"F0.wireOp",EDGE,"E0.bottom");Q22=makeQuery(id+"F11.boolean.opBoolean","INTERSECT",EDGE,{"derivedFrom":[makeQuery(id+"F9.opFillet","SPLIT",FACE,{"disambiguationData":[OD(3.0)],"derivedFrom":makeQuery(id+"F8.opFillet","MERGE",FACE,{"derivedFrom":[makeQuery(id+"F7.boolean.opBoolean","SPLIT",FACE,{"disambiguationData":[TD([makeQuery(id+"F1.opExtrude","CAP_FACE",FACE,{"disambiguationData":[OSD([subQ22,subQ21,subQ3,subQ16])],"isStart":false})])],"derivedFrom":subQ14}),makeQuery(id+"F7.boolean.opBoolean","SPLIT",FACE,{"disambiguationData":[TD([makeQuery(id+"F1.opExtrude","CAP_FACE",FACE,{"disambiguationData":[OSD([subQ22,subQ21,subQ3,subQ16])],"isStart":true})])],"derivedFrom":subQ14}),makeQuery(id+"F7.boolean.opBoolean","SPLIT",FACE,{"disambiguationData":[TD([subQ17])],"derivedFrom":subQ14}),makeQuery(id+"F7.boolean.opBoolean","SPLIT",FACE,{"disambiguationData":[TD([subQ4])],"derivedFrom":subQ14})]})}),makeQuery(id+"F11.opExtrude","SWEPT_FACE",FACE,{"disambiguationData":[OSD([sQuery(id+"F10.wireOp",EDGE,"E8.1.2.1")])]})]});}
            var Q23;
            {var subQ1=makeQuery(id+"F5.opExtrude","SWEPT_FACE",FACE,{"disambiguationData":[OSD([sQuery(id+"F4.wireOp",EDGE,"E2.top")])]});var subQ2=makeQuery(id+"F3.boolean.opBoolean","COPY",FACE,{"derivedFrom":makeQuery(id+"F3.opExtrude","SWEPT_FACE",FACE,{"disambiguationData":[OSD([sQuery(id+"F2.wireOp",EDGE,"E1.top")])]})});var subQ3=sQuery(id+"F0.wireOp",EDGE,"E0.left");var subQ4=makeQuery(id+"F1.opExtrude","SWEPT_FACE",FACE,{"disambiguationData":[OSD([subQ3])]});var subQ14=makeQuery(id+"F5.boolean.opBoolean","MERGE",FACE,{"derivedFrom":[subQ2,subQ1]});var subQ16=sQuery(id+"F0.wireOp",EDGE,"E0.right");var subQ17=makeQuery(id+"F1.opExtrude","SWEPT_FACE",FACE,{"disambiguationData":[OSD([subQ16])]});var subQ21=sQuery(id+"F0.wireOp",EDGE,"E0.top");var subQ22=sQuery(id+"F0.wireOp",EDGE,"E0.bottom");Q23=makeQuery(id+"F11.boolean.opBoolean","INTERSECT",EDGE,{"derivedFrom":[makeQuery(id+"F9.opFillet","SPLIT",FACE,{"disambiguationData":[OD(3.0)],"derivedFrom":makeQuery(id+"F8.opFillet","MERGE",FACE,{"derivedFrom":[makeQuery(id+"F7.boolean.opBoolean","SPLIT",FACE,{"disambiguationData":[TD([makeQuery(id+"F1.opExtrude","CAP_FACE",FACE,{"disambiguationData":[OSD([subQ22,subQ21,subQ3,subQ16])],"isStart":false})])],"derivedFrom":subQ14}),makeQuery(id+"F7.boolean.opBoolean","SPLIT",FACE,{"disambiguationData":[TD([makeQuery(id+"F1.opExtrude","CAP_FACE",FACE,{"disambiguationData":[OSD([subQ22,subQ21,subQ3,subQ16])],"isStart":true})])],"derivedFrom":subQ14}),makeQuery(id+"F7.boolean.opBoolean","SPLIT",FACE,{"disambiguationData":[TD([subQ17])],"derivedFrom":subQ14}),makeQuery(id+"F7.boolean.opBoolean","SPLIT",FACE,{"disambiguationData":[TD([subQ4])],"derivedFrom":subQ14})]})}),makeQuery(id+"F11.opExtrude","SWEPT_FACE",FACE,{"disambiguationData":[OSD([sQuery(id+"F10.wireOp",EDGE,"E8.1.1.1")])]})]});}
            var Q24;
            {var subQ1=makeQuery(id+"F5.opExtrude","SWEPT_FACE",FACE,{"disambiguationData":[OSD([sQuery(id+"F4.wireOp",EDGE,"E2.top")])]});var subQ2=makeQuery(id+"F3.boolean.opBoolean","COPY",FACE,{"derivedFrom":makeQuery(id+"F3.opExtrude","SWEPT_FACE",FACE,{"disambiguationData":[OSD([sQuery(id+"F2.wireOp",EDGE,"E1.top")])]})});var subQ3=sQuery(id+"F0.wireOp",EDGE,"E0.left");var subQ4=makeQuery(id+"F1.opExtrude","SWEPT_FACE",FACE,{"disambiguationData":[OSD([subQ3])]});var subQ14=makeQuery(id+"F5.boolean.opBoolean","MERGE",FACE,{"derivedFrom":[subQ2,subQ1]});var subQ16=sQuery(id+"F0.wireOp",EDGE,"E0.right");var subQ17=makeQuery(id+"F1.opExtrude","SWEPT_FACE",FACE,{"disambiguationData":[OSD([subQ16])]});var subQ21=sQuery(id+"F0.wireOp",EDGE,"E0.top");var subQ22=sQuery(id+"F0.wireOp",EDGE,"E0.bottom");Q24=makeQuery(id+"F11.boolean.opBoolean","INTERSECT",EDGE,{"derivedFrom":[makeQuery(id+"F9.opFillet","SPLIT",FACE,{"disambiguationData":[OD(3.0)],"derivedFrom":makeQuery(id+"F8.opFillet","MERGE",FACE,{"derivedFrom":[makeQuery(id+"F7.boolean.opBoolean","SPLIT",FACE,{"disambiguationData":[TD([makeQuery(id+"F1.opExtrude","CAP_FACE",FACE,{"disambiguationData":[OSD([subQ22,subQ21,subQ3,subQ16])],"isStart":false})])],"derivedFrom":subQ14}),makeQuery(id+"F7.boolean.opBoolean","SPLIT",FACE,{"disambiguationData":[TD([makeQuery(id+"F1.opExtrude","CAP_FACE",FACE,{"disambiguationData":[OSD([subQ22,subQ21,subQ3,subQ16])],"isStart":true})])],"derivedFrom":subQ14}),makeQuery(id+"F7.boolean.opBoolean","SPLIT",FACE,{"disambiguationData":[TD([subQ17])],"derivedFrom":subQ14}),makeQuery(id+"F7.boolean.opBoolean","SPLIT",FACE,{"disambiguationData":[TD([subQ4])],"derivedFrom":subQ14})]})}),makeQuery(id+"F11.opExtrude","SWEPT_FACE",FACE,{"disambiguationData":[OSD([sQuery(id+"F10.wireOp",EDGE,"E8.1.0.1")])]})]});}
            var Q25;
            {var subQ0=makeQuery(id+"F5.opExtrude","SWEPT_FACE",FACE,{"disambiguationData":[OSD([sQuery(id+"F4.wireOp",EDGE,"E2.bottom")])]});var subQ2=makeQuery(id+"F3.boolean.opBoolean","COPY",FACE,{"derivedFrom":makeQuery(id+"F3.opExtrude","SWEPT_FACE",FACE,{"disambiguationData":[OSD([sQuery(id+"F2.wireOp",EDGE,"E1.bottom")])]})});var subQ3=sQuery(id+"F0.wireOp",EDGE,"E0.left");var subQ4=makeQuery(id+"F1.opExtrude","SWEPT_FACE",FACE,{"disambiguationData":[OSD([subQ3])]});var subQ14=makeQuery(id+"F5.boolean.opBoolean","MERGE",FACE,{"derivedFrom":[subQ2,subQ0]});var subQ16=sQuery(id+"F0.wireOp",EDGE,"E0.right");var subQ17=makeQuery(id+"F1.opExtrude","SWEPT_FACE",FACE,{"disambiguationData":[OSD([subQ16])]});var subQ21=sQuery(id+"F0.wireOp",EDGE,"E0.top");var subQ22=sQuery(id+"F0.wireOp",EDGE,"E0.bottom");Q25=makeQuery(id+"F11.boolean.opBoolean","INTERSECT",EDGE,{"derivedFrom":[makeQuery(id+"F9.opFillet","SPLIT",FACE,{"disambiguationData":[OD(3.0)],"derivedFrom":makeQuery(id+"F8.opFillet","MERGE",FACE,{"derivedFrom":[makeQuery(id+"F7.boolean.opBoolean","SPLIT",FACE,{"disambiguationData":[TD([makeQuery(id+"F1.opExtrude","CAP_FACE",FACE,{"disambiguationData":[OSD([subQ22,subQ21,subQ3,subQ16])],"isStart":false})])],"derivedFrom":subQ14}),makeQuery(id+"F7.boolean.opBoolean","SPLIT",FACE,{"disambiguationData":[TD([makeQuery(id+"F1.opExtrude","CAP_FACE",FACE,{"disambiguationData":[OSD([subQ22,subQ21,subQ3,subQ16])],"isStart":true})])],"derivedFrom":subQ14}),makeQuery(id+"F7.boolean.opBoolean","SPLIT",FACE,{"disambiguationData":[TD([subQ17])],"derivedFrom":subQ14}),makeQuery(id+"F7.boolean.opBoolean","SPLIT",FACE,{"disambiguationData":[TD([subQ4])],"derivedFrom":subQ14})]})}),makeQuery(id+"F11.opExtrude","SWEPT_FACE",FACE,{"disambiguationData":[OSD([sQuery(id+"F10.wireOp",EDGE,"E8.1.0.1")])]})]});}
            var Q26;
            {var subQ0=makeQuery(id+"F5.opExtrude","SWEPT_FACE",FACE,{"disambiguationData":[OSD([sQuery(id+"F4.wireOp",EDGE,"E2.bottom")])]});var subQ2=makeQuery(id+"F3.boolean.opBoolean","COPY",FACE,{"derivedFrom":makeQuery(id+"F3.opExtrude","SWEPT_FACE",FACE,{"disambiguationData":[OSD([sQuery(id+"F2.wireOp",EDGE,"E1.bottom")])]})});var subQ3=sQuery(id+"F0.wireOp",EDGE,"E0.left");var subQ4=makeQuery(id+"F1.opExtrude","SWEPT_FACE",FACE,{"disambiguationData":[OSD([subQ3])]});var subQ14=makeQuery(id+"F5.boolean.opBoolean","MERGE",FACE,{"derivedFrom":[subQ2,subQ0]});var subQ16=sQuery(id+"F0.wireOp",EDGE,"E0.right");var subQ17=makeQuery(id+"F1.opExtrude","SWEPT_FACE",FACE,{"disambiguationData":[OSD([subQ16])]});var subQ21=sQuery(id+"F0.wireOp",EDGE,"E0.top");var subQ22=sQuery(id+"F0.wireOp",EDGE,"E0.bottom");Q26=makeQuery(id+"F11.boolean.opBoolean","INTERSECT",EDGE,{"derivedFrom":[makeQuery(id+"F9.opFillet","SPLIT",FACE,{"disambiguationData":[OD(3.0)],"derivedFrom":makeQuery(id+"F8.opFillet","MERGE",FACE,{"derivedFrom":[makeQuery(id+"F7.boolean.opBoolean","SPLIT",FACE,{"disambiguationData":[TD([makeQuery(id+"F1.opExtrude","CAP_FACE",FACE,{"disambiguationData":[OSD([subQ22,subQ21,subQ3,subQ16])],"isStart":false})])],"derivedFrom":subQ14}),makeQuery(id+"F7.boolean.opBoolean","SPLIT",FACE,{"disambiguationData":[TD([makeQuery(id+"F1.opExtrude","CAP_FACE",FACE,{"disambiguationData":[OSD([subQ22,subQ21,subQ3,subQ16])],"isStart":true})])],"derivedFrom":subQ14}),makeQuery(id+"F7.boolean.opBoolean","SPLIT",FACE,{"disambiguationData":[TD([subQ17])],"derivedFrom":subQ14}),makeQuery(id+"F7.boolean.opBoolean","SPLIT",FACE,{"disambiguationData":[TD([subQ4])],"derivedFrom":subQ14})]})}),makeQuery(id+"F11.opExtrude","SWEPT_FACE",FACE,{"disambiguationData":[OSD([sQuery(id+"F10.wireOp",EDGE,"E8.1.1.1")])]})]});}
            var Q27;
            {var subQ0=makeQuery(id+"F5.opExtrude","SWEPT_FACE",FACE,{"disambiguationData":[OSD([sQuery(id+"F4.wireOp",EDGE,"E2.bottom")])]});var subQ2=makeQuery(id+"F3.boolean.opBoolean","COPY",FACE,{"derivedFrom":makeQuery(id+"F3.opExtrude","SWEPT_FACE",FACE,{"disambiguationData":[OSD([sQuery(id+"F2.wireOp",EDGE,"E1.bottom")])]})});var subQ3=sQuery(id+"F0.wireOp",EDGE,"E0.left");var subQ4=makeQuery(id+"F1.opExtrude","SWEPT_FACE",FACE,{"disambiguationData":[OSD([subQ3])]});var subQ14=makeQuery(id+"F5.boolean.opBoolean","MERGE",FACE,{"derivedFrom":[subQ2,subQ0]});var subQ16=sQuery(id+"F0.wireOp",EDGE,"E0.right");var subQ17=makeQuery(id+"F1.opExtrude","SWEPT_FACE",FACE,{"disambiguationData":[OSD([subQ16])]});var subQ21=sQuery(id+"F0.wireOp",EDGE,"E0.top");var subQ22=sQuery(id+"F0.wireOp",EDGE,"E0.bottom");Q27=makeQuery(id+"F11.boolean.opBoolean","INTERSECT",EDGE,{"derivedFrom":[makeQuery(id+"F9.opFillet","SPLIT",FACE,{"disambiguationData":[OD(3.0)],"derivedFrom":makeQuery(id+"F8.opFillet","MERGE",FACE,{"derivedFrom":[makeQuery(id+"F7.boolean.opBoolean","SPLIT",FACE,{"disambiguationData":[TD([makeQuery(id+"F1.opExtrude","CAP_FACE",FACE,{"disambiguationData":[OSD([subQ22,subQ21,subQ3,subQ16])],"isStart":false})])],"derivedFrom":subQ14}),makeQuery(id+"F7.boolean.opBoolean","SPLIT",FACE,{"disambiguationData":[TD([makeQuery(id+"F1.opExtrude","CAP_FACE",FACE,{"disambiguationData":[OSD([subQ22,subQ21,subQ3,subQ16])],"isStart":true})])],"derivedFrom":subQ14}),makeQuery(id+"F7.boolean.opBoolean","SPLIT",FACE,{"disambiguationData":[TD([subQ17])],"derivedFrom":subQ14}),makeQuery(id+"F7.boolean.opBoolean","SPLIT",FACE,{"disambiguationData":[TD([subQ4])],"derivedFrom":subQ14})]})}),makeQuery(id+"F11.opExtrude","SWEPT_FACE",FACE,{"disambiguationData":[OSD([sQuery(id+"F10.wireOp",EDGE,"E8.1.2.1")])]})]});}
            var Q28;
            {var subQ0=makeQuery(id+"F5.opExtrude","SWEPT_FACE",FACE,{"disambiguationData":[OSD([sQuery(id+"F4.wireOp",EDGE,"E2.bottom")])]});var subQ2=makeQuery(id+"F3.boolean.opBoolean","COPY",FACE,{"derivedFrom":makeQuery(id+"F3.opExtrude","SWEPT_FACE",FACE,{"disambiguationData":[OSD([sQuery(id+"F2.wireOp",EDGE,"E1.bottom")])]})});var subQ3=sQuery(id+"F0.wireOp",EDGE,"E0.left");var subQ4=makeQuery(id+"F1.opExtrude","SWEPT_FACE",FACE,{"disambiguationData":[OSD([subQ3])]});var subQ14=makeQuery(id+"F5.boolean.opBoolean","MERGE",FACE,{"derivedFrom":[subQ2,subQ0]});var subQ16=sQuery(id+"F0.wireOp",EDGE,"E0.right");var subQ17=makeQuery(id+"F1.opExtrude","SWEPT_FACE",FACE,{"disambiguationData":[OSD([subQ16])]});var subQ21=sQuery(id+"F0.wireOp",EDGE,"E0.top");var subQ22=sQuery(id+"F0.wireOp",EDGE,"E0.bottom");Q28=makeQuery(id+"F11.boolean.opBoolean","INTERSECT",EDGE,{"derivedFrom":[makeQuery(id+"F9.opFillet","SPLIT",FACE,{"disambiguationData":[OD(1.0)],"derivedFrom":makeQuery(id+"F8.opFillet","MERGE",FACE,{"derivedFrom":[makeQuery(id+"F7.boolean.opBoolean","SPLIT",FACE,{"disambiguationData":[TD([makeQuery(id+"F1.opExtrude","CAP_FACE",FACE,{"disambiguationData":[OSD([subQ22,subQ21,subQ3,subQ16])],"isStart":false})])],"derivedFrom":subQ14}),makeQuery(id+"F7.boolean.opBoolean","SPLIT",FACE,{"disambiguationData":[TD([makeQuery(id+"F1.opExtrude","CAP_FACE",FACE,{"disambiguationData":[OSD([subQ22,subQ21,subQ3,subQ16])],"isStart":true})])],"derivedFrom":subQ14}),makeQuery(id+"F7.boolean.opBoolean","SPLIT",FACE,{"disambiguationData":[TD([subQ17])],"derivedFrom":subQ14}),makeQuery(id+"F7.boolean.opBoolean","SPLIT",FACE,{"disambiguationData":[TD([subQ4])],"derivedFrom":subQ14})]})}),makeQuery(id+"F11.opExtrude","SWEPT_FACE",FACE,{"disambiguationData":[OSD([sQuery(id+"F10.wireOp",EDGE,"E6.0.1.2")])]})]});}
            var Q29;
            {var subQ0=makeQuery(id+"F5.opExtrude","SWEPT_FACE",FACE,{"disambiguationData":[OSD([sQuery(id+"F4.wireOp",EDGE,"E2.bottom")])]});var subQ2=makeQuery(id+"F3.boolean.opBoolean","COPY",FACE,{"derivedFrom":makeQuery(id+"F3.opExtrude","SWEPT_FACE",FACE,{"disambiguationData":[OSD([sQuery(id+"F2.wireOp",EDGE,"E1.bottom")])]})});var subQ3=sQuery(id+"F0.wireOp",EDGE,"E0.left");var subQ4=makeQuery(id+"F1.opExtrude","SWEPT_FACE",FACE,{"disambiguationData":[OSD([subQ3])]});var subQ14=makeQuery(id+"F5.boolean.opBoolean","MERGE",FACE,{"derivedFrom":[subQ2,subQ0]});var subQ16=sQuery(id+"F0.wireOp",EDGE,"E0.right");var subQ17=makeQuery(id+"F1.opExtrude","SWEPT_FACE",FACE,{"disambiguationData":[OSD([subQ16])]});var subQ21=sQuery(id+"F0.wireOp",EDGE,"E0.top");var subQ22=sQuery(id+"F0.wireOp",EDGE,"E0.bottom");Q29=makeQuery(id+"F11.boolean.opBoolean","INTERSECT",EDGE,{"derivedFrom":[makeQuery(id+"F9.opFillet","SPLIT",FACE,{"disambiguationData":[OD(1.0)],"derivedFrom":makeQuery(id+"F8.opFillet","MERGE",FACE,{"derivedFrom":[makeQuery(id+"F7.boolean.opBoolean","SPLIT",FACE,{"disambiguationData":[TD([makeQuery(id+"F1.opExtrude","CAP_FACE",FACE,{"disambiguationData":[OSD([subQ22,subQ21,subQ3,subQ16])],"isStart":false})])],"derivedFrom":subQ14}),makeQuery(id+"F7.boolean.opBoolean","SPLIT",FACE,{"disambiguationData":[TD([makeQuery(id+"F1.opExtrude","CAP_FACE",FACE,{"disambiguationData":[OSD([subQ22,subQ21,subQ3,subQ16])],"isStart":true})])],"derivedFrom":subQ14}),makeQuery(id+"F7.boolean.opBoolean","SPLIT",FACE,{"disambiguationData":[TD([subQ17])],"derivedFrom":subQ14}),makeQuery(id+"F7.boolean.opBoolean","SPLIT",FACE,{"disambiguationData":[TD([subQ4])],"derivedFrom":subQ14})]})}),makeQuery(id+"F11.opExtrude","SWEPT_FACE",FACE,{"disambiguationData":[OSD([sQuery(id+"F10.wireOp",EDGE,"E6.0.1.14")])]})]});}
            var Q30;
            {var subQ1=makeQuery(id+"F5.opExtrude","SWEPT_FACE",FACE,{"disambiguationData":[OSD([sQuery(id+"F4.wireOp",EDGE,"E2.top")])]});var subQ2=makeQuery(id+"F3.boolean.opBoolean","COPY",FACE,{"derivedFrom":makeQuery(id+"F3.opExtrude","SWEPT_FACE",FACE,{"disambiguationData":[OSD([sQuery(id+"F2.wireOp",EDGE,"E1.top")])]})});var subQ3=sQuery(id+"F0.wireOp",EDGE,"E0.left");var subQ4=makeQuery(id+"F1.opExtrude","SWEPT_FACE",FACE,{"disambiguationData":[OSD([subQ3])]});var subQ14=makeQuery(id+"F5.boolean.opBoolean","MERGE",FACE,{"derivedFrom":[subQ2,subQ1]});var subQ16=sQuery(id+"F0.wireOp",EDGE,"E0.right");var subQ17=makeQuery(id+"F1.opExtrude","SWEPT_FACE",FACE,{"disambiguationData":[OSD([subQ16])]});var subQ21=sQuery(id+"F0.wireOp",EDGE,"E0.top");var subQ22=sQuery(id+"F0.wireOp",EDGE,"E0.bottom");Q30=makeQuery(id+"F11.boolean.opBoolean","INTERSECT",EDGE,{"derivedFrom":[makeQuery(id+"F9.opFillet","SPLIT",FACE,{"disambiguationData":[OD(3.0)],"derivedFrom":makeQuery(id+"F8.opFillet","MERGE",FACE,{"derivedFrom":[makeQuery(id+"F7.boolean.opBoolean","SPLIT",FACE,{"disambiguationData":[TD([makeQuery(id+"F1.opExtrude","CAP_FACE",FACE,{"disambiguationData":[OSD([subQ22,subQ21,subQ3,subQ16])],"isStart":false})])],"derivedFrom":subQ14}),makeQuery(id+"F7.boolean.opBoolean","SPLIT",FACE,{"disambiguationData":[TD([makeQuery(id+"F1.opExtrude","CAP_FACE",FACE,{"disambiguationData":[OSD([subQ22,subQ21,subQ3,subQ16])],"isStart":true})])],"derivedFrom":subQ14}),makeQuery(id+"F7.boolean.opBoolean","SPLIT",FACE,{"disambiguationData":[TD([subQ17])],"derivedFrom":subQ14}),makeQuery(id+"F7.boolean.opBoolean","SPLIT",FACE,{"disambiguationData":[TD([subQ4])],"derivedFrom":subQ14})]})}),makeQuery(id+"F11.opExtrude","SWEPT_FACE",FACE,{"disambiguationData":[OSD([sQuery(id+"F10.wireOp",EDGE,"E8.1.2.0")])]})]});}
            var Q31;
            {var subQ1=makeQuery(id+"F5.opExtrude","SWEPT_FACE",FACE,{"disambiguationData":[OSD([sQuery(id+"F4.wireOp",EDGE,"E2.top")])]});var subQ2=makeQuery(id+"F3.boolean.opBoolean","COPY",FACE,{"derivedFrom":makeQuery(id+"F3.opExtrude","SWEPT_FACE",FACE,{"disambiguationData":[OSD([sQuery(id+"F2.wireOp",EDGE,"E1.top")])]})});var subQ3=sQuery(id+"F0.wireOp",EDGE,"E0.left");var subQ4=makeQuery(id+"F1.opExtrude","SWEPT_FACE",FACE,{"disambiguationData":[OSD([subQ3])]});var subQ14=makeQuery(id+"F5.boolean.opBoolean","MERGE",FACE,{"derivedFrom":[subQ2,subQ1]});var subQ16=sQuery(id+"F0.wireOp",EDGE,"E0.right");var subQ17=makeQuery(id+"F1.opExtrude","SWEPT_FACE",FACE,{"disambiguationData":[OSD([subQ16])]});var subQ21=sQuery(id+"F0.wireOp",EDGE,"E0.top");var subQ22=sQuery(id+"F0.wireOp",EDGE,"E0.bottom");Q31=makeQuery(id+"F11.boolean.opBoolean","INTERSECT",EDGE,{"derivedFrom":[makeQuery(id+"F9.opFillet","SPLIT",FACE,{"disambiguationData":[OD(3.0)],"derivedFrom":makeQuery(id+"F8.opFillet","MERGE",FACE,{"derivedFrom":[makeQuery(id+"F7.boolean.opBoolean","SPLIT",FACE,{"disambiguationData":[TD([makeQuery(id+"F1.opExtrude","CAP_FACE",FACE,{"disambiguationData":[OSD([subQ22,subQ21,subQ3,subQ16])],"isStart":false})])],"derivedFrom":subQ14}),makeQuery(id+"F7.boolean.opBoolean","SPLIT",FACE,{"disambiguationData":[TD([makeQuery(id+"F1.opExtrude","CAP_FACE",FACE,{"disambiguationData":[OSD([subQ22,subQ21,subQ3,subQ16])],"isStart":true})])],"derivedFrom":subQ14}),makeQuery(id+"F7.boolean.opBoolean","SPLIT",FACE,{"disambiguationData":[TD([subQ17])],"derivedFrom":subQ14}),makeQuery(id+"F7.boolean.opBoolean","SPLIT",FACE,{"disambiguationData":[TD([subQ4])],"derivedFrom":subQ14})]})}),makeQuery(id+"F11.opExtrude","SWEPT_FACE",FACE,{"disambiguationData":[OSD([sQuery(id+"F10.wireOp",EDGE,"E8.1.1.0")])]})]});}
            var Q32;
            {var subQ1=makeQuery(id+"F5.opExtrude","SWEPT_FACE",FACE,{"disambiguationData":[OSD([sQuery(id+"F4.wireOp",EDGE,"E2.top")])]});var subQ2=makeQuery(id+"F3.boolean.opBoolean","COPY",FACE,{"derivedFrom":makeQuery(id+"F3.opExtrude","SWEPT_FACE",FACE,{"disambiguationData":[OSD([sQuery(id+"F2.wireOp",EDGE,"E1.top")])]})});var subQ3=sQuery(id+"F0.wireOp",EDGE,"E0.left");var subQ4=makeQuery(id+"F1.opExtrude","SWEPT_FACE",FACE,{"disambiguationData":[OSD([subQ3])]});var subQ14=makeQuery(id+"F5.boolean.opBoolean","MERGE",FACE,{"derivedFrom":[subQ2,subQ1]});var subQ16=sQuery(id+"F0.wireOp",EDGE,"E0.right");var subQ17=makeQuery(id+"F1.opExtrude","SWEPT_FACE",FACE,{"disambiguationData":[OSD([subQ16])]});var subQ21=sQuery(id+"F0.wireOp",EDGE,"E0.top");var subQ22=sQuery(id+"F0.wireOp",EDGE,"E0.bottom");Q32=makeQuery(id+"F11.boolean.opBoolean","INTERSECT",EDGE,{"derivedFrom":[makeQuery(id+"F9.opFillet","SPLIT",FACE,{"disambiguationData":[OD(3.0)],"derivedFrom":makeQuery(id+"F8.opFillet","MERGE",FACE,{"derivedFrom":[makeQuery(id+"F7.boolean.opBoolean","SPLIT",FACE,{"disambiguationData":[TD([makeQuery(id+"F1.opExtrude","CAP_FACE",FACE,{"disambiguationData":[OSD([subQ22,subQ21,subQ3,subQ16])],"isStart":false})])],"derivedFrom":subQ14}),makeQuery(id+"F7.boolean.opBoolean","SPLIT",FACE,{"disambiguationData":[TD([makeQuery(id+"F1.opExtrude","CAP_FACE",FACE,{"disambiguationData":[OSD([subQ22,subQ21,subQ3,subQ16])],"isStart":true})])],"derivedFrom":subQ14}),makeQuery(id+"F7.boolean.opBoolean","SPLIT",FACE,{"disambiguationData":[TD([subQ17])],"derivedFrom":subQ14}),makeQuery(id+"F7.boolean.opBoolean","SPLIT",FACE,{"disambiguationData":[TD([subQ4])],"derivedFrom":subQ14})]})}),makeQuery(id+"F11.opExtrude","SWEPT_FACE",FACE,{"disambiguationData":[OSD([sQuery(id+"F10.wireOp",EDGE,"E8.1.0.0")])]})]});}
            var Q33;
            {var subQ0=makeQuery(id+"F5.opExtrude","SWEPT_FACE",FACE,{"disambiguationData":[OSD([sQuery(id+"F4.wireOp",EDGE,"E2.bottom")])]});var subQ2=makeQuery(id+"F3.boolean.opBoolean","COPY",FACE,{"derivedFrom":makeQuery(id+"F3.opExtrude","SWEPT_FACE",FACE,{"disambiguationData":[OSD([sQuery(id+"F2.wireOp",EDGE,"E1.bottom")])]})});var subQ3=sQuery(id+"F0.wireOp",EDGE,"E0.left");var subQ4=makeQuery(id+"F1.opExtrude","SWEPT_FACE",FACE,{"disambiguationData":[OSD([subQ3])]});var subQ14=makeQuery(id+"F5.boolean.opBoolean","MERGE",FACE,{"derivedFrom":[subQ2,subQ0]});var subQ16=sQuery(id+"F0.wireOp",EDGE,"E0.right");var subQ17=makeQuery(id+"F1.opExtrude","SWEPT_FACE",FACE,{"disambiguationData":[OSD([subQ16])]});var subQ21=sQuery(id+"F0.wireOp",EDGE,"E0.top");var subQ22=sQuery(id+"F0.wireOp",EDGE,"E0.bottom");Q33=makeQuery(id+"F11.boolean.opBoolean","INTERSECT",EDGE,{"derivedFrom":[makeQuery(id+"F9.opFillet","SPLIT",FACE,{"disambiguationData":[OD(3.0)],"derivedFrom":makeQuery(id+"F8.opFillet","MERGE",FACE,{"derivedFrom":[makeQuery(id+"F7.boolean.opBoolean","SPLIT",FACE,{"disambiguationData":[TD([makeQuery(id+"F1.opExtrude","CAP_FACE",FACE,{"disambiguationData":[OSD([subQ22,subQ21,subQ3,subQ16])],"isStart":false})])],"derivedFrom":subQ14}),makeQuery(id+"F7.boolean.opBoolean","SPLIT",FACE,{"disambiguationData":[TD([makeQuery(id+"F1.opExtrude","CAP_FACE",FACE,{"disambiguationData":[OSD([subQ22,subQ21,subQ3,subQ16])],"isStart":true})])],"derivedFrom":subQ14}),makeQuery(id+"F7.boolean.opBoolean","SPLIT",FACE,{"disambiguationData":[TD([subQ17])],"derivedFrom":subQ14}),makeQuery(id+"F7.boolean.opBoolean","SPLIT",FACE,{"disambiguationData":[TD([subQ4])],"derivedFrom":subQ14})]})}),makeQuery(id+"F11.opExtrude","SWEPT_FACE",FACE,{"disambiguationData":[OSD([sQuery(id+"F10.wireOp",EDGE,"E8.1.0.0")])]})]});}
            var Q34;
            {var subQ0=makeQuery(id+"F5.opExtrude","SWEPT_FACE",FACE,{"disambiguationData":[OSD([sQuery(id+"F4.wireOp",EDGE,"E2.bottom")])]});var subQ2=makeQuery(id+"F3.boolean.opBoolean","COPY",FACE,{"derivedFrom":makeQuery(id+"F3.opExtrude","SWEPT_FACE",FACE,{"disambiguationData":[OSD([sQuery(id+"F2.wireOp",EDGE,"E1.bottom")])]})});var subQ3=sQuery(id+"F0.wireOp",EDGE,"E0.left");var subQ4=makeQuery(id+"F1.opExtrude","SWEPT_FACE",FACE,{"disambiguationData":[OSD([subQ3])]});var subQ14=makeQuery(id+"F5.boolean.opBoolean","MERGE",FACE,{"derivedFrom":[subQ2,subQ0]});var subQ16=sQuery(id+"F0.wireOp",EDGE,"E0.right");var subQ17=makeQuery(id+"F1.opExtrude","SWEPT_FACE",FACE,{"disambiguationData":[OSD([subQ16])]});var subQ21=sQuery(id+"F0.wireOp",EDGE,"E0.top");var subQ22=sQuery(id+"F0.wireOp",EDGE,"E0.bottom");Q34=makeQuery(id+"F11.boolean.opBoolean","INTERSECT",EDGE,{"derivedFrom":[makeQuery(id+"F9.opFillet","SPLIT",FACE,{"disambiguationData":[OD(3.0)],"derivedFrom":makeQuery(id+"F8.opFillet","MERGE",FACE,{"derivedFrom":[makeQuery(id+"F7.boolean.opBoolean","SPLIT",FACE,{"disambiguationData":[TD([makeQuery(id+"F1.opExtrude","CAP_FACE",FACE,{"disambiguationData":[OSD([subQ22,subQ21,subQ3,subQ16])],"isStart":false})])],"derivedFrom":subQ14}),makeQuery(id+"F7.boolean.opBoolean","SPLIT",FACE,{"disambiguationData":[TD([makeQuery(id+"F1.opExtrude","CAP_FACE",FACE,{"disambiguationData":[OSD([subQ22,subQ21,subQ3,subQ16])],"isStart":true})])],"derivedFrom":subQ14}),makeQuery(id+"F7.boolean.opBoolean","SPLIT",FACE,{"disambiguationData":[TD([subQ17])],"derivedFrom":subQ14}),makeQuery(id+"F7.boolean.opBoolean","SPLIT",FACE,{"disambiguationData":[TD([subQ4])],"derivedFrom":subQ14})]})}),makeQuery(id+"F11.opExtrude","SWEPT_FACE",FACE,{"disambiguationData":[OSD([sQuery(id+"F10.wireOp",EDGE,"E8.1.1.0")])]})]});}
            var Q35;
            {var subQ0=makeQuery(id+"F5.opExtrude","SWEPT_FACE",FACE,{"disambiguationData":[OSD([sQuery(id+"F4.wireOp",EDGE,"E2.bottom")])]});var subQ2=makeQuery(id+"F3.boolean.opBoolean","COPY",FACE,{"derivedFrom":makeQuery(id+"F3.opExtrude","SWEPT_FACE",FACE,{"disambiguationData":[OSD([sQuery(id+"F2.wireOp",EDGE,"E1.bottom")])]})});var subQ3=sQuery(id+"F0.wireOp",EDGE,"E0.left");var subQ4=makeQuery(id+"F1.opExtrude","SWEPT_FACE",FACE,{"disambiguationData":[OSD([subQ3])]});var subQ14=makeQuery(id+"F5.boolean.opBoolean","MERGE",FACE,{"derivedFrom":[subQ2,subQ0]});var subQ16=sQuery(id+"F0.wireOp",EDGE,"E0.right");var subQ17=makeQuery(id+"F1.opExtrude","SWEPT_FACE",FACE,{"disambiguationData":[OSD([subQ16])]});var subQ21=sQuery(id+"F0.wireOp",EDGE,"E0.top");var subQ22=sQuery(id+"F0.wireOp",EDGE,"E0.bottom");Q35=makeQuery(id+"F11.boolean.opBoolean","INTERSECT",EDGE,{"derivedFrom":[makeQuery(id+"F9.opFillet","SPLIT",FACE,{"disambiguationData":[OD(3.0)],"derivedFrom":makeQuery(id+"F8.opFillet","MERGE",FACE,{"derivedFrom":[makeQuery(id+"F7.boolean.opBoolean","SPLIT",FACE,{"disambiguationData":[TD([makeQuery(id+"F1.opExtrude","CAP_FACE",FACE,{"disambiguationData":[OSD([subQ22,subQ21,subQ3,subQ16])],"isStart":false})])],"derivedFrom":subQ14}),makeQuery(id+"F7.boolean.opBoolean","SPLIT",FACE,{"disambiguationData":[TD([makeQuery(id+"F1.opExtrude","CAP_FACE",FACE,{"disambiguationData":[OSD([subQ22,subQ21,subQ3,subQ16])],"isStart":true})])],"derivedFrom":subQ14}),makeQuery(id+"F7.boolean.opBoolean","SPLIT",FACE,{"disambiguationData":[TD([subQ17])],"derivedFrom":subQ14}),makeQuery(id+"F7.boolean.opBoolean","SPLIT",FACE,{"disambiguationData":[TD([subQ4])],"derivedFrom":subQ14})]})}),makeQuery(id+"F11.opExtrude","SWEPT_FACE",FACE,{"disambiguationData":[OSD([sQuery(id+"F10.wireOp",EDGE,"E8.1.2.0")])]})]});}
            var Q36;
            {var subQ0=makeQuery(id+"F5.opExtrude","SWEPT_FACE",FACE,{"disambiguationData":[OSD([sQuery(id+"F4.wireOp",EDGE,"E2.bottom")])]});var subQ2=makeQuery(id+"F3.boolean.opBoolean","COPY",FACE,{"derivedFrom":makeQuery(id+"F3.opExtrude","SWEPT_FACE",FACE,{"disambiguationData":[OSD([sQuery(id+"F2.wireOp",EDGE,"E1.bottom")])]})});var subQ3=sQuery(id+"F0.wireOp",EDGE,"E0.left");var subQ4=makeQuery(id+"F1.opExtrude","SWEPT_FACE",FACE,{"disambiguationData":[OSD([subQ3])]});var subQ14=makeQuery(id+"F5.boolean.opBoolean","MERGE",FACE,{"derivedFrom":[subQ2,subQ0]});var subQ16=sQuery(id+"F0.wireOp",EDGE,"E0.right");var subQ17=makeQuery(id+"F1.opExtrude","SWEPT_FACE",FACE,{"disambiguationData":[OSD([subQ16])]});var subQ21=sQuery(id+"F0.wireOp",EDGE,"E0.top");var subQ22=sQuery(id+"F0.wireOp",EDGE,"E0.bottom");Q36=makeQuery(id+"F11.boolean.opBoolean","INTERSECT",EDGE,{"derivedFrom":[makeQuery(id+"F9.opFillet","SPLIT",FACE,{"disambiguationData":[OD(1.0)],"derivedFrom":makeQuery(id+"F8.opFillet","MERGE",FACE,{"derivedFrom":[makeQuery(id+"F7.boolean.opBoolean","SPLIT",FACE,{"disambiguationData":[TD([makeQuery(id+"F1.opExtrude","CAP_FACE",FACE,{"disambiguationData":[OSD([subQ22,subQ21,subQ3,subQ16])],"isStart":false})])],"derivedFrom":subQ14}),makeQuery(id+"F7.boolean.opBoolean","SPLIT",FACE,{"disambiguationData":[TD([makeQuery(id+"F1.opExtrude","CAP_FACE",FACE,{"disambiguationData":[OSD([subQ22,subQ21,subQ3,subQ16])],"isStart":true})])],"derivedFrom":subQ14}),makeQuery(id+"F7.boolean.opBoolean","SPLIT",FACE,{"disambiguationData":[TD([subQ17])],"derivedFrom":subQ14}),makeQuery(id+"F7.boolean.opBoolean","SPLIT",FACE,{"disambiguationData":[TD([subQ4])],"derivedFrom":subQ14})]})}),makeQuery(id+"F11.opExtrude","SWEPT_FACE",FACE,{"disambiguationData":[OSD([sQuery(id+"F10.wireOp",EDGE,"E6.0.1.16")])]})]});}
            var Q37;
            {var subQ1=makeQuery(id+"F5.opExtrude","SWEPT_FACE",FACE,{"disambiguationData":[OSD([sQuery(id+"F4.wireOp",EDGE,"E2.top")])]});var subQ2=makeQuery(id+"F3.boolean.opBoolean","COPY",FACE,{"derivedFrom":makeQuery(id+"F3.opExtrude","SWEPT_FACE",FACE,{"disambiguationData":[OSD([sQuery(id+"F2.wireOp",EDGE,"E1.top")])]})});var subQ3=sQuery(id+"F0.wireOp",EDGE,"E0.left");var subQ4=makeQuery(id+"F1.opExtrude","SWEPT_FACE",FACE,{"disambiguationData":[OSD([subQ3])]});var subQ14=makeQuery(id+"F5.boolean.opBoolean","MERGE",FACE,{"derivedFrom":[subQ2,subQ1]});var subQ16=sQuery(id+"F0.wireOp",EDGE,"E0.right");var subQ17=makeQuery(id+"F1.opExtrude","SWEPT_FACE",FACE,{"disambiguationData":[OSD([subQ16])]});var subQ21=sQuery(id+"F0.wireOp",EDGE,"E0.top");var subQ22=sQuery(id+"F0.wireOp",EDGE,"E0.bottom");Q37=makeQuery(id+"F11.boolean.opBoolean","INTERSECT",EDGE,{"derivedFrom":[makeQuery(id+"F9.opFillet","SPLIT",FACE,{"disambiguationData":[OD(1.0)],"derivedFrom":makeQuery(id+"F8.opFillet","MERGE",FACE,{"derivedFrom":[makeQuery(id+"F7.boolean.opBoolean","SPLIT",FACE,{"disambiguationData":[TD([makeQuery(id+"F1.opExtrude","CAP_FACE",FACE,{"disambiguationData":[OSD([subQ22,subQ21,subQ3,subQ16])],"isStart":false})])],"derivedFrom":subQ14}),makeQuery(id+"F7.boolean.opBoolean","SPLIT",FACE,{"disambiguationData":[TD([makeQuery(id+"F1.opExtrude","CAP_FACE",FACE,{"disambiguationData":[OSD([subQ22,subQ21,subQ3,subQ16])],"isStart":true})])],"derivedFrom":subQ14}),makeQuery(id+"F7.boolean.opBoolean","SPLIT",FACE,{"disambiguationData":[TD([subQ17])],"derivedFrom":subQ14}),makeQuery(id+"F7.boolean.opBoolean","SPLIT",FACE,{"disambiguationData":[TD([subQ4])],"derivedFrom":subQ14})]})}),makeQuery(id+"F11.opExtrude","SWEPT_FACE",FACE,{"disambiguationData":[OSD([sQuery(id+"F10.wireOp",EDGE,"E6.0.1.16")])]})]});}
            var Q38;
            {var subQ1=makeQuery(id+"F5.opExtrude","SWEPT_FACE",FACE,{"disambiguationData":[OSD([sQuery(id+"F4.wireOp",EDGE,"E2.top")])]});var subQ2=makeQuery(id+"F3.boolean.opBoolean","COPY",FACE,{"derivedFrom":makeQuery(id+"F3.opExtrude","SWEPT_FACE",FACE,{"disambiguationData":[OSD([sQuery(id+"F2.wireOp",EDGE,"E1.top")])]})});var subQ3=sQuery(id+"F0.wireOp",EDGE,"E0.left");var subQ4=makeQuery(id+"F1.opExtrude","SWEPT_FACE",FACE,{"disambiguationData":[OSD([subQ3])]});var subQ14=makeQuery(id+"F5.boolean.opBoolean","MERGE",FACE,{"derivedFrom":[subQ2,subQ1]});var subQ16=sQuery(id+"F0.wireOp",EDGE,"E0.right");var subQ17=makeQuery(id+"F1.opExtrude","SWEPT_FACE",FACE,{"disambiguationData":[OSD([subQ16])]});var subQ21=sQuery(id+"F0.wireOp",EDGE,"E0.top");var subQ22=sQuery(id+"F0.wireOp",EDGE,"E0.bottom");Q38=makeQuery(id+"F11.boolean.opBoolean","INTERSECT",EDGE,{"derivedFrom":[makeQuery(id+"F9.opFillet","SPLIT",FACE,{"disambiguationData":[OD(1.0)],"derivedFrom":makeQuery(id+"F8.opFillet","MERGE",FACE,{"derivedFrom":[makeQuery(id+"F7.boolean.opBoolean","SPLIT",FACE,{"disambiguationData":[TD([makeQuery(id+"F1.opExtrude","CAP_FACE",FACE,{"disambiguationData":[OSD([subQ22,subQ21,subQ3,subQ16])],"isStart":false})])],"derivedFrom":subQ14}),makeQuery(id+"F7.boolean.opBoolean","SPLIT",FACE,{"disambiguationData":[TD([makeQuery(id+"F1.opExtrude","CAP_FACE",FACE,{"disambiguationData":[OSD([subQ22,subQ21,subQ3,subQ16])],"isStart":true})])],"derivedFrom":subQ14}),makeQuery(id+"F7.boolean.opBoolean","SPLIT",FACE,{"disambiguationData":[TD([subQ17])],"derivedFrom":subQ14}),makeQuery(id+"F7.boolean.opBoolean","SPLIT",FACE,{"disambiguationData":[TD([subQ4])],"derivedFrom":subQ14})]})}),makeQuery(id+"F11.opExtrude","SWEPT_FACE",FACE,{"disambiguationData":[OSD([sQuery(id+"F10.wireOp",EDGE,"E6.0.1.14")])]})]});}
            var Q39;
            {var subQ1=makeQuery(id+"F5.opExtrude","SWEPT_FACE",FACE,{"disambiguationData":[OSD([sQuery(id+"F4.wireOp",EDGE,"E2.top")])]});var subQ2=makeQuery(id+"F3.boolean.opBoolean","COPY",FACE,{"derivedFrom":makeQuery(id+"F3.opExtrude","SWEPT_FACE",FACE,{"disambiguationData":[OSD([sQuery(id+"F2.wireOp",EDGE,"E1.top")])]})});var subQ3=sQuery(id+"F0.wireOp",EDGE,"E0.left");var subQ4=makeQuery(id+"F1.opExtrude","SWEPT_FACE",FACE,{"disambiguationData":[OSD([subQ3])]});var subQ14=makeQuery(id+"F5.boolean.opBoolean","MERGE",FACE,{"derivedFrom":[subQ2,subQ1]});var subQ16=sQuery(id+"F0.wireOp",EDGE,"E0.right");var subQ17=makeQuery(id+"F1.opExtrude","SWEPT_FACE",FACE,{"disambiguationData":[OSD([subQ16])]});var subQ21=sQuery(id+"F0.wireOp",EDGE,"E0.top");var subQ22=sQuery(id+"F0.wireOp",EDGE,"E0.bottom");Q39=makeQuery(id+"F11.boolean.opBoolean","INTERSECT",EDGE,{"derivedFrom":[makeQuery(id+"F9.opFillet","SPLIT",FACE,{"disambiguationData":[OD(1.0)],"derivedFrom":makeQuery(id+"F8.opFillet","MERGE",FACE,{"derivedFrom":[makeQuery(id+"F7.boolean.opBoolean","SPLIT",FACE,{"disambiguationData":[TD([makeQuery(id+"F1.opExtrude","CAP_FACE",FACE,{"disambiguationData":[OSD([subQ22,subQ21,subQ3,subQ16])],"isStart":false})])],"derivedFrom":subQ14}),makeQuery(id+"F7.boolean.opBoolean","SPLIT",FACE,{"disambiguationData":[TD([makeQuery(id+"F1.opExtrude","CAP_FACE",FACE,{"disambiguationData":[OSD([subQ22,subQ21,subQ3,subQ16])],"isStart":true})])],"derivedFrom":subQ14}),makeQuery(id+"F7.boolean.opBoolean","SPLIT",FACE,{"disambiguationData":[TD([subQ17])],"derivedFrom":subQ14}),makeQuery(id+"F7.boolean.opBoolean","SPLIT",FACE,{"disambiguationData":[TD([subQ4])],"derivedFrom":subQ14})]})}),makeQuery(id+"F11.opExtrude","SWEPT_FACE",FACE,{"disambiguationData":[OSD([sQuery(id+"F10.wireOp",EDGE,"E6.0.1.2")])]})]});}
            var Q40;
            {var subQ0=makeQuery(id+"F5.opExtrude","SWEPT_FACE",FACE,{"disambiguationData":[OSD([sQuery(id+"F4.wireOp",EDGE,"E2.bottom")])]});var subQ2=makeQuery(id+"F3.boolean.opBoolean","COPY",FACE,{"derivedFrom":makeQuery(id+"F3.opExtrude","SWEPT_FACE",FACE,{"disambiguationData":[OSD([sQuery(id+"F2.wireOp",EDGE,"E1.bottom")])]})});var subQ3=sQuery(id+"F0.wireOp",EDGE,"E0.left");var subQ4=makeQuery(id+"F1.opExtrude","SWEPT_FACE",FACE,{"disambiguationData":[OSD([subQ3])]});var subQ14=makeQuery(id+"F5.boolean.opBoolean","MERGE",FACE,{"derivedFrom":[subQ2,subQ0]});var subQ16=sQuery(id+"F0.wireOp",EDGE,"E0.right");var subQ17=makeQuery(id+"F1.opExtrude","SWEPT_FACE",FACE,{"disambiguationData":[OSD([subQ16])]});var subQ21=sQuery(id+"F0.wireOp",EDGE,"E0.top");var subQ22=sQuery(id+"F0.wireOp",EDGE,"E0.bottom");Q40=makeQuery(id+"F11.boolean.opBoolean","INTERSECT",EDGE,{"derivedFrom":[makeQuery(id+"F9.opFillet","SPLIT",FACE,{"disambiguationData":[OD(1.0)],"derivedFrom":makeQuery(id+"F8.opFillet","MERGE",FACE,{"derivedFrom":[makeQuery(id+"F7.boolean.opBoolean","SPLIT",FACE,{"disambiguationData":[TD([makeQuery(id+"F1.opExtrude","CAP_FACE",FACE,{"disambiguationData":[OSD([subQ22,subQ21,subQ3,subQ16])],"isStart":false})])],"derivedFrom":subQ14}),makeQuery(id+"F7.boolean.opBoolean","SPLIT",FACE,{"disambiguationData":[TD([makeQuery(id+"F1.opExtrude","CAP_FACE",FACE,{"disambiguationData":[OSD([subQ22,subQ21,subQ3,subQ16])],"isStart":true})])],"derivedFrom":subQ14}),makeQuery(id+"F7.boolean.opBoolean","SPLIT",FACE,{"disambiguationData":[TD([subQ17])],"derivedFrom":subQ14}),makeQuery(id+"F7.boolean.opBoolean","SPLIT",FACE,{"disambiguationData":[TD([subQ4])],"derivedFrom":subQ14})]})}),makeQuery(id+"F11.opExtrude","SWEPT_FACE",FACE,{"disambiguationData":[OSD([sQuery(id+"F10.wireOp",EDGE,"E6.0.1.3")])]})]});}
            var Q41;
            {var subQ1=makeQuery(id+"F5.opExtrude","SWEPT_FACE",FACE,{"disambiguationData":[OSD([sQuery(id+"F4.wireOp",EDGE,"E2.top")])]});var subQ2=makeQuery(id+"F3.boolean.opBoolean","COPY",FACE,{"derivedFrom":makeQuery(id+"F3.opExtrude","SWEPT_FACE",FACE,{"disambiguationData":[OSD([sQuery(id+"F2.wireOp",EDGE,"E1.top")])]})});var subQ3=sQuery(id+"F0.wireOp",EDGE,"E0.left");var subQ4=makeQuery(id+"F1.opExtrude","SWEPT_FACE",FACE,{"disambiguationData":[OSD([subQ3])]});var subQ14=makeQuery(id+"F5.boolean.opBoolean","MERGE",FACE,{"derivedFrom":[subQ2,subQ1]});var subQ16=sQuery(id+"F0.wireOp",EDGE,"E0.right");var subQ17=makeQuery(id+"F1.opExtrude","SWEPT_FACE",FACE,{"disambiguationData":[OSD([subQ16])]});var subQ21=sQuery(id+"F0.wireOp",EDGE,"E0.top");var subQ22=sQuery(id+"F0.wireOp",EDGE,"E0.bottom");Q41=makeQuery(id+"F11.boolean.opBoolean","INTERSECT",EDGE,{"derivedFrom":[makeQuery(id+"F9.opFillet","SPLIT",FACE,{"disambiguationData":[OD(1.0)],"derivedFrom":makeQuery(id+"F8.opFillet","MERGE",FACE,{"derivedFrom":[makeQuery(id+"F7.boolean.opBoolean","SPLIT",FACE,{"disambiguationData":[TD([makeQuery(id+"F1.opExtrude","CAP_FACE",FACE,{"disambiguationData":[OSD([subQ22,subQ21,subQ3,subQ16])],"isStart":false})])],"derivedFrom":subQ14}),makeQuery(id+"F7.boolean.opBoolean","SPLIT",FACE,{"disambiguationData":[TD([makeQuery(id+"F1.opExtrude","CAP_FACE",FACE,{"disambiguationData":[OSD([subQ22,subQ21,subQ3,subQ16])],"isStart":true})])],"derivedFrom":subQ14}),makeQuery(id+"F7.boolean.opBoolean","SPLIT",FACE,{"disambiguationData":[TD([subQ17])],"derivedFrom":subQ14}),makeQuery(id+"F7.boolean.opBoolean","SPLIT",FACE,{"disambiguationData":[TD([subQ4])],"derivedFrom":subQ14})]})}),makeQuery(id+"F11.opExtrude","SWEPT_FACE",FACE,{"disambiguationData":[OSD([sQuery(id+"F10.wireOp",EDGE,"E6.0.1.3")])]})]});}
            var Q42;
            {var subQ1=makeQuery(id+"F5.opExtrude","SWEPT_FACE",FACE,{"disambiguationData":[OSD([sQuery(id+"F4.wireOp",EDGE,"E2.top")])]});var subQ2=makeQuery(id+"F3.boolean.opBoolean","COPY",FACE,{"derivedFrom":makeQuery(id+"F3.opExtrude","SWEPT_FACE",FACE,{"disambiguationData":[OSD([sQuery(id+"F2.wireOp",EDGE,"E1.top")])]})});var subQ3=sQuery(id+"F0.wireOp",EDGE,"E0.left");var subQ4=makeQuery(id+"F1.opExtrude","SWEPT_FACE",FACE,{"disambiguationData":[OSD([subQ3])]});var subQ14=makeQuery(id+"F5.boolean.opBoolean","MERGE",FACE,{"derivedFrom":[subQ2,subQ1]});var subQ16=sQuery(id+"F0.wireOp",EDGE,"E0.right");var subQ17=makeQuery(id+"F1.opExtrude","SWEPT_FACE",FACE,{"disambiguationData":[OSD([subQ16])]});var subQ21=sQuery(id+"F0.wireOp",EDGE,"E0.top");var subQ22=sQuery(id+"F0.wireOp",EDGE,"E0.bottom");Q42=makeQuery(id+"F11.boolean.opBoolean","INTERSECT",EDGE,{"derivedFrom":[makeQuery(id+"F9.opFillet","SPLIT",FACE,{"disambiguationData":[OD(2.0)],"derivedFrom":makeQuery(id+"F8.opFillet","MERGE",FACE,{"derivedFrom":[makeQuery(id+"F7.boolean.opBoolean","SPLIT",FACE,{"disambiguationData":[TD([makeQuery(id+"F1.opExtrude","CAP_FACE",FACE,{"disambiguationData":[OSD([subQ22,subQ21,subQ3,subQ16])],"isStart":false})])],"derivedFrom":subQ14}),makeQuery(id+"F7.boolean.opBoolean","SPLIT",FACE,{"disambiguationData":[TD([makeQuery(id+"F1.opExtrude","CAP_FACE",FACE,{"disambiguationData":[OSD([subQ22,subQ21,subQ3,subQ16])],"isStart":true})])],"derivedFrom":subQ14}),makeQuery(id+"F7.boolean.opBoolean","SPLIT",FACE,{"disambiguationData":[TD([subQ17])],"derivedFrom":subQ14}),makeQuery(id+"F7.boolean.opBoolean","SPLIT",FACE,{"disambiguationData":[TD([subQ4])],"derivedFrom":subQ14})]})}),makeQuery(id+"F11.opExtrude","SWEPT_FACE",FACE,{"disambiguationData":[OSD([sQuery(id+"F10.wireOp",EDGE,"E7.top")])]})]});}
            var Q43;
            {var subQ1=makeQuery(id+"F5.opExtrude","SWEPT_FACE",FACE,{"disambiguationData":[OSD([sQuery(id+"F4.wireOp",EDGE,"E2.top")])]});var subQ2=makeQuery(id+"F3.boolean.opBoolean","COPY",FACE,{"derivedFrom":makeQuery(id+"F3.opExtrude","SWEPT_FACE",FACE,{"disambiguationData":[OSD([sQuery(id+"F2.wireOp",EDGE,"E1.top")])]})});var subQ3=sQuery(id+"F0.wireOp",EDGE,"E0.left");var subQ4=makeQuery(id+"F1.opExtrude","SWEPT_FACE",FACE,{"disambiguationData":[OSD([subQ3])]});var subQ14=makeQuery(id+"F5.boolean.opBoolean","MERGE",FACE,{"derivedFrom":[subQ2,subQ1]});var subQ16=sQuery(id+"F0.wireOp",EDGE,"E0.right");var subQ17=makeQuery(id+"F1.opExtrude","SWEPT_FACE",FACE,{"disambiguationData":[OSD([subQ16])]});var subQ21=sQuery(id+"F0.wireOp",EDGE,"E0.top");var subQ22=sQuery(id+"F0.wireOp",EDGE,"E0.bottom");Q43=makeQuery(id+"F11.boolean.opBoolean","INTERSECT",EDGE,{"derivedFrom":[makeQuery(id+"F9.opFillet","SPLIT",FACE,{"disambiguationData":[OD(2.0)],"derivedFrom":makeQuery(id+"F8.opFillet","MERGE",FACE,{"derivedFrom":[makeQuery(id+"F7.boolean.opBoolean","SPLIT",FACE,{"disambiguationData":[TD([makeQuery(id+"F1.opExtrude","CAP_FACE",FACE,{"disambiguationData":[OSD([subQ22,subQ21,subQ3,subQ16])],"isStart":false})])],"derivedFrom":subQ14}),makeQuery(id+"F7.boolean.opBoolean","SPLIT",FACE,{"disambiguationData":[TD([makeQuery(id+"F1.opExtrude","CAP_FACE",FACE,{"disambiguationData":[OSD([subQ22,subQ21,subQ3,subQ16])],"isStart":true})])],"derivedFrom":subQ14}),makeQuery(id+"F7.boolean.opBoolean","SPLIT",FACE,{"disambiguationData":[TD([subQ17])],"derivedFrom":subQ14}),makeQuery(id+"F7.boolean.opBoolean","SPLIT",FACE,{"disambiguationData":[TD([subQ4])],"derivedFrom":subQ14})]})}),makeQuery(id+"F11.opExtrude","SWEPT_FACE",FACE,{"disambiguationData":[OSD([sQuery(id+"F10.wireOp",EDGE,"E8.0.1.0")])]})]});}
            var Q44;
            {var subQ1=makeQuery(id+"F5.opExtrude","SWEPT_FACE",FACE,{"disambiguationData":[OSD([sQuery(id+"F4.wireOp",EDGE,"E2.top")])]});var subQ2=makeQuery(id+"F3.boolean.opBoolean","COPY",FACE,{"derivedFrom":makeQuery(id+"F3.opExtrude","SWEPT_FACE",FACE,{"disambiguationData":[OSD([sQuery(id+"F2.wireOp",EDGE,"E1.top")])]})});var subQ3=sQuery(id+"F0.wireOp",EDGE,"E0.left");var subQ4=makeQuery(id+"F1.opExtrude","SWEPT_FACE",FACE,{"disambiguationData":[OSD([subQ3])]});var subQ14=makeQuery(id+"F5.boolean.opBoolean","MERGE",FACE,{"derivedFrom":[subQ2,subQ1]});var subQ16=sQuery(id+"F0.wireOp",EDGE,"E0.right");var subQ17=makeQuery(id+"F1.opExtrude","SWEPT_FACE",FACE,{"disambiguationData":[OSD([subQ16])]});var subQ21=sQuery(id+"F0.wireOp",EDGE,"E0.top");var subQ22=sQuery(id+"F0.wireOp",EDGE,"E0.bottom");Q44=makeQuery(id+"F11.boolean.opBoolean","INTERSECT",EDGE,{"derivedFrom":[makeQuery(id+"F9.opFillet","SPLIT",FACE,{"disambiguationData":[OD(2.0)],"derivedFrom":makeQuery(id+"F8.opFillet","MERGE",FACE,{"derivedFrom":[makeQuery(id+"F7.boolean.opBoolean","SPLIT",FACE,{"disambiguationData":[TD([makeQuery(id+"F1.opExtrude","CAP_FACE",FACE,{"disambiguationData":[OSD([subQ22,subQ21,subQ3,subQ16])],"isStart":false})])],"derivedFrom":subQ14}),makeQuery(id+"F7.boolean.opBoolean","SPLIT",FACE,{"disambiguationData":[TD([makeQuery(id+"F1.opExtrude","CAP_FACE",FACE,{"disambiguationData":[OSD([subQ22,subQ21,subQ3,subQ16])],"isStart":true})])],"derivedFrom":subQ14}),makeQuery(id+"F7.boolean.opBoolean","SPLIT",FACE,{"disambiguationData":[TD([subQ17])],"derivedFrom":subQ14}),makeQuery(id+"F7.boolean.opBoolean","SPLIT",FACE,{"disambiguationData":[TD([subQ4])],"derivedFrom":subQ14})]})}),makeQuery(id+"F11.opExtrude","SWEPT_FACE",FACE,{"disambiguationData":[OSD([sQuery(id+"F10.wireOp",EDGE,"E8.0.2.0")])]})]});}
            var Q45;
            {var subQ0=makeQuery(id+"F5.opExtrude","SWEPT_FACE",FACE,{"disambiguationData":[OSD([sQuery(id+"F4.wireOp",EDGE,"E2.bottom")])]});var subQ2=makeQuery(id+"F3.boolean.opBoolean","COPY",FACE,{"derivedFrom":makeQuery(id+"F3.opExtrude","SWEPT_FACE",FACE,{"disambiguationData":[OSD([sQuery(id+"F2.wireOp",EDGE,"E1.bottom")])]})});var subQ3=sQuery(id+"F0.wireOp",EDGE,"E0.left");var subQ4=makeQuery(id+"F1.opExtrude","SWEPT_FACE",FACE,{"disambiguationData":[OSD([subQ3])]});var subQ14=makeQuery(id+"F5.boolean.opBoolean","MERGE",FACE,{"derivedFrom":[subQ2,subQ0]});var subQ16=sQuery(id+"F0.wireOp",EDGE,"E0.right");var subQ17=makeQuery(id+"F1.opExtrude","SWEPT_FACE",FACE,{"disambiguationData":[OSD([subQ16])]});var subQ21=sQuery(id+"F0.wireOp",EDGE,"E0.top");var subQ22=sQuery(id+"F0.wireOp",EDGE,"E0.bottom");Q45=makeQuery(id+"F11.boolean.opBoolean","INTERSECT",EDGE,{"derivedFrom":[makeQuery(id+"F9.opFillet","SPLIT",FACE,{"disambiguationData":[OD(2.0)],"derivedFrom":makeQuery(id+"F8.opFillet","MERGE",FACE,{"derivedFrom":[makeQuery(id+"F7.boolean.opBoolean","SPLIT",FACE,{"disambiguationData":[TD([makeQuery(id+"F1.opExtrude","CAP_FACE",FACE,{"disambiguationData":[OSD([subQ22,subQ21,subQ3,subQ16])],"isStart":false})])],"derivedFrom":subQ14}),makeQuery(id+"F7.boolean.opBoolean","SPLIT",FACE,{"disambiguationData":[TD([makeQuery(id+"F1.opExtrude","CAP_FACE",FACE,{"disambiguationData":[OSD([subQ22,subQ21,subQ3,subQ16])],"isStart":true})])],"derivedFrom":subQ14}),makeQuery(id+"F7.boolean.opBoolean","SPLIT",FACE,{"disambiguationData":[TD([subQ17])],"derivedFrom":subQ14}),makeQuery(id+"F7.boolean.opBoolean","SPLIT",FACE,{"disambiguationData":[TD([subQ4])],"derivedFrom":subQ14})]})}),makeQuery(id+"F11.opExtrude","SWEPT_FACE",FACE,{"disambiguationData":[OSD([sQuery(id+"F10.wireOp",EDGE,"E7.top")])]})]});}
            var Q46;
            {var subQ0=makeQuery(id+"F5.opExtrude","SWEPT_FACE",FACE,{"disambiguationData":[OSD([sQuery(id+"F4.wireOp",EDGE,"E2.bottom")])]});var subQ2=makeQuery(id+"F3.boolean.opBoolean","COPY",FACE,{"derivedFrom":makeQuery(id+"F3.opExtrude","SWEPT_FACE",FACE,{"disambiguationData":[OSD([sQuery(id+"F2.wireOp",EDGE,"E1.bottom")])]})});var subQ3=sQuery(id+"F0.wireOp",EDGE,"E0.left");var subQ4=makeQuery(id+"F1.opExtrude","SWEPT_FACE",FACE,{"disambiguationData":[OSD([subQ3])]});var subQ14=makeQuery(id+"F5.boolean.opBoolean","MERGE",FACE,{"derivedFrom":[subQ2,subQ0]});var subQ16=sQuery(id+"F0.wireOp",EDGE,"E0.right");var subQ17=makeQuery(id+"F1.opExtrude","SWEPT_FACE",FACE,{"disambiguationData":[OSD([subQ16])]});var subQ21=sQuery(id+"F0.wireOp",EDGE,"E0.top");var subQ22=sQuery(id+"F0.wireOp",EDGE,"E0.bottom");Q46=makeQuery(id+"F11.boolean.opBoolean","INTERSECT",EDGE,{"derivedFrom":[makeQuery(id+"F9.opFillet","SPLIT",FACE,{"disambiguationData":[OD(2.0)],"derivedFrom":makeQuery(id+"F8.opFillet","MERGE",FACE,{"derivedFrom":[makeQuery(id+"F7.boolean.opBoolean","SPLIT",FACE,{"disambiguationData":[TD([makeQuery(id+"F1.opExtrude","CAP_FACE",FACE,{"disambiguationData":[OSD([subQ22,subQ21,subQ3,subQ16])],"isStart":false})])],"derivedFrom":subQ14}),makeQuery(id+"F7.boolean.opBoolean","SPLIT",FACE,{"disambiguationData":[TD([makeQuery(id+"F1.opExtrude","CAP_FACE",FACE,{"disambiguationData":[OSD([subQ22,subQ21,subQ3,subQ16])],"isStart":true})])],"derivedFrom":subQ14}),makeQuery(id+"F7.boolean.opBoolean","SPLIT",FACE,{"disambiguationData":[TD([subQ17])],"derivedFrom":subQ14}),makeQuery(id+"F7.boolean.opBoolean","SPLIT",FACE,{"disambiguationData":[TD([subQ4])],"derivedFrom":subQ14})]})}),makeQuery(id+"F11.opExtrude","SWEPT_FACE",FACE,{"disambiguationData":[OSD([sQuery(id+"F10.wireOp",EDGE,"E8.0.1.0")])]})]});}
            var Q47;
            {var subQ0=makeQuery(id+"F5.opExtrude","SWEPT_FACE",FACE,{"disambiguationData":[OSD([sQuery(id+"F4.wireOp",EDGE,"E2.bottom")])]});var subQ2=makeQuery(id+"F3.boolean.opBoolean","COPY",FACE,{"derivedFrom":makeQuery(id+"F3.opExtrude","SWEPT_FACE",FACE,{"disambiguationData":[OSD([sQuery(id+"F2.wireOp",EDGE,"E1.bottom")])]})});var subQ3=sQuery(id+"F0.wireOp",EDGE,"E0.left");var subQ4=makeQuery(id+"F1.opExtrude","SWEPT_FACE",FACE,{"disambiguationData":[OSD([subQ3])]});var subQ14=makeQuery(id+"F5.boolean.opBoolean","MERGE",FACE,{"derivedFrom":[subQ2,subQ0]});var subQ16=sQuery(id+"F0.wireOp",EDGE,"E0.right");var subQ17=makeQuery(id+"F1.opExtrude","SWEPT_FACE",FACE,{"disambiguationData":[OSD([subQ16])]});var subQ21=sQuery(id+"F0.wireOp",EDGE,"E0.top");var subQ22=sQuery(id+"F0.wireOp",EDGE,"E0.bottom");Q47=makeQuery(id+"F11.boolean.opBoolean","INTERSECT",EDGE,{"derivedFrom":[makeQuery(id+"F9.opFillet","SPLIT",FACE,{"disambiguationData":[OD(2.0)],"derivedFrom":makeQuery(id+"F8.opFillet","MERGE",FACE,{"derivedFrom":[makeQuery(id+"F7.boolean.opBoolean","SPLIT",FACE,{"disambiguationData":[TD([makeQuery(id+"F1.opExtrude","CAP_FACE",FACE,{"disambiguationData":[OSD([subQ22,subQ21,subQ3,subQ16])],"isStart":false})])],"derivedFrom":subQ14}),makeQuery(id+"F7.boolean.opBoolean","SPLIT",FACE,{"disambiguationData":[TD([makeQuery(id+"F1.opExtrude","CAP_FACE",FACE,{"disambiguationData":[OSD([subQ22,subQ21,subQ3,subQ16])],"isStart":true})])],"derivedFrom":subQ14}),makeQuery(id+"F7.boolean.opBoolean","SPLIT",FACE,{"disambiguationData":[TD([subQ17])],"derivedFrom":subQ14}),makeQuery(id+"F7.boolean.opBoolean","SPLIT",FACE,{"disambiguationData":[TD([subQ4])],"derivedFrom":subQ14})]})}),makeQuery(id+"F11.opExtrude","SWEPT_FACE",FACE,{"disambiguationData":[OSD([sQuery(id+"F10.wireOp",EDGE,"E8.0.2.0")])]})]});}
            fillet(context, id + "F12", {"entities" : qUnion([Q0, Q1, Q2, Q3, Q4, Q5, Q6, Q7, Q8, Q9, Q10, Q11, Q12, Q13, Q14, Q15, Q16, Q17, Q18, Q19, Q20, Q21, Q22, Q23, Q24, Q25, Q26, Q27, Q28, Q29, Q30, Q31, Q32, Q33, Q34, Q35, Q36, Q37, Q38, Q39, Q40, Q41, Q42, Q43, Q44, Q45, Q46, Q47]), "radius" : 5 * mm, "tangentPropagation" : true, "allowEdgeOverflow" : false});
        }
    });
